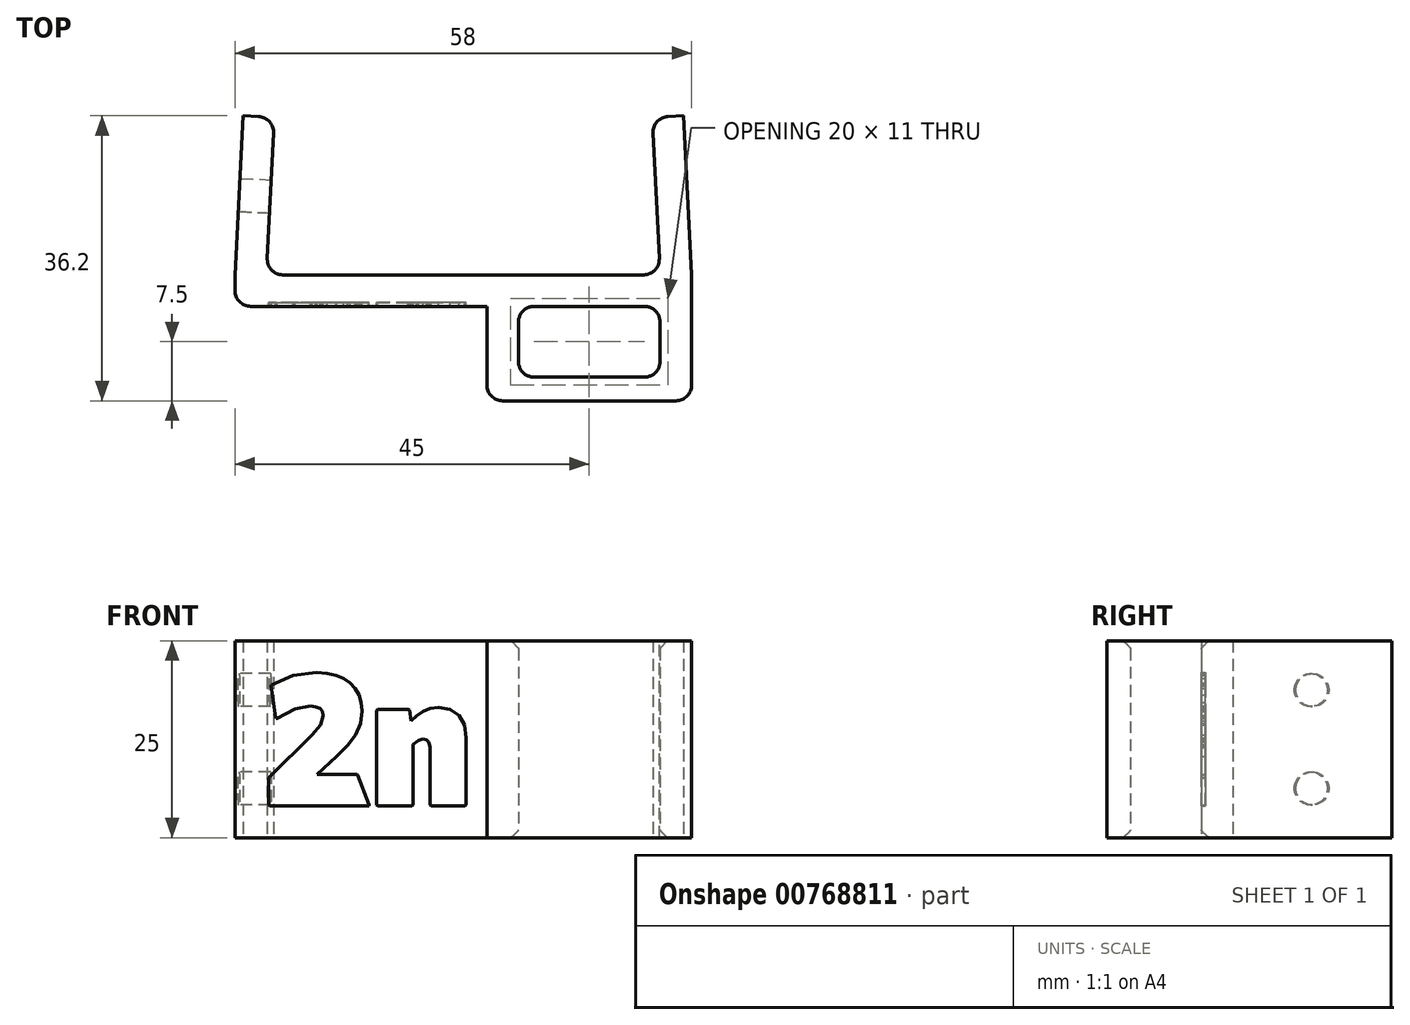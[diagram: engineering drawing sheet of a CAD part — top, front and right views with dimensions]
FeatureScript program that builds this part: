
annotation { "Feature Type Name" : "Feature", "Feature Type Description" : "" }
export const myFeature = defineFeature(function(context is Context, id is Id, definition is map)
    precondition{}
    {
        {
            var Q0;
            Q0=qCreatedBy(makeId("Top.planeOp"),FACE);
            var sketch = newSketch(context, id + "F0", { "sketchPlane" : qUnion([Q0])});
            skLineSegment(sketch, "E0", {"start": v(0, 0) * mm, "end": v(-25, 0) * mm});
            skLineSegment(sketch, "E1", {"start": v(-25, 0) * mm, "end": v(-24, 20) * mm});
            skLineSegment(sketch, "E2", {"start": v(0, 0) * mm, "end": v(0, 58.1) * mm, "construction": true});
            skLineSegment(sketch, "E3", {"start": v(-24, 20) * mm, "end": v(-28, 20.2) * mm});
            skLineSegment(sketch, "E4", {"start": v(-28, 20.2) * mm, "end": v(-29, 0) * mm});
            skLineSegment(sketch, "E5", {"start": v(-29, 0) * mm, "end": v(-29, -4) * mm});
            skLineSegment(sketch, "E6", {"start": v(-29, -4) * mm, "end": v(0, -4) * mm});
            skLineSegment(sketch, "E7.MirrorCS", {"start": v(25, 0) * mm, "end": v(24, 20) * mm});
            skLineSegment(sketch, "E8.MirrorCS", {"start": v(24, 20) * mm, "end": v(28, 20.2) * mm});
            skLineSegment(sketch, "E9.MirrorCS", {"start": v(28, 20.2) * mm, "end": v(29, 0) * mm});
            skLineSegment(sketch, "E10.MirrorCS", {"start": v(0, 0) * mm, "end": v(25, 0) * mm});
            skLineSegment(sketch, "E11.MirrorCS", {"start": v(29, 0) * mm, "end": v(29, -4) * mm});
            skPoint(sketch, "E12", {"position": v(25, -4) * mm});
            skPoint(sketch, "E13.second.point", {"position": v(10.6, -3) * mm});
            skPoint(sketch, "E13.third.point", {"position": v(18.98, -11.3) * mm});
            skLineSegment(sketch, "E14.trimOffspring", {"start": v(3, -4) * mm, "end": v(0, -4) * mm});
            skPoint(sketch, "E15.orphan", {"position": v(29, -4) * mm});
            skPoint(sketch, "E16", {"position": v(16, -3) * mm});
            skLineSegment(sketch, "E17", {"start": v(7, -4) * mm, "end": v(25, -4) * mm});
            skLineSegment(sketch, "E18", {"start": v(3, -4) * mm, "end": v(3, -16) * mm});
            skPoint(sketch, "E18.endSnap0", {"position": v(15, -16) * mm});
            skLineSegment(sketch, "E19", {"start": v(3, -16) * mm, "end": v(29, -16) * mm});
            skLineSegment(sketch, "E20", {"start": v(29, -4) * mm, "end": v(29, -16) * mm});
            skLineSegment(sketch, "E21", {"start": v(25, -4) * mm, "end": v(25, -13) * mm});
            skPoint(sketch, "E21.endSnap0", {"position": v(16, -13) * mm});
            skLineSegment(sketch, "E22", {"start": v(25, -13) * mm, "end": v(7, -13) * mm});
            skLineSegment(sketch, "E23", {"start": v(7, -13) * mm, "end": v(7, -4) * mm});
            skSolve(sketch);
        }
        {
            var Q0;
            Q0=makeQuery(id+"F0.imprint","IMPRINT",FACE,{"disambiguationData":[TD([[makeQuery(id+"F0.imprint","IMPRINT",EDGE,{"derivedFrom":sQuery(id+"F0.wireOp",EDGE,"E0")}),1.0]])]});
            extrude(context, id + "F1", {"entities" : qUnion([Q0]), "depth" : 25 * mm, "offsetDistance" : 25 * mm});
        }
        {
            var Q0;
            Q0=makeQuery(id+"F1.opExtrude","SWEPT_EDGE",EDGE,{"disambiguationData":[OSD([sQuery(id+"F0.wireOp",EDGE,"E0"),sQuery(id+"F0.wireOp",EDGE,"E1")])]});
            var Q1;
            Q1=makeQuery(id+"F1.opExtrude","SWEPT_EDGE",EDGE,{"disambiguationData":[OSD([sQuery(id+"F0.wireOp",EDGE,"E1"),sQuery(id+"F0.wireOp",EDGE,"E3")])]});
            var Q2;
            Q2=makeQuery(id+"F1.opExtrude","SWEPT_EDGE",EDGE,{"disambiguationData":[OSD([sQuery(id+"F0.wireOp",EDGE,"E7.MirrorCS"),sQuery(id+"F0.wireOp",EDGE,"E10.MirrorCS")])]});
            var Q3;
            Q3=makeQuery(id+"F1.opExtrude","SWEPT_EDGE",EDGE,{"disambiguationData":[OSD([sQuery(id+"F0.wireOp",EDGE,"E7.MirrorCS"),sQuery(id+"F0.wireOp",EDGE,"E8.MirrorCS")])]});
            var Q4;
            Q4=makeQuery(id+"F1.opExtrude","SWEPT_EDGE",EDGE,{"disambiguationData":[OSD([sQuery(id+"F0.wireOp",EDGE,"E5"),sQuery(id+"F0.wireOp",EDGE,"E6")])]});
            var Q5;
            Q5=makeQuery(id+"F1.opExtrude","SWEPT_EDGE",EDGE,{"disambiguationData":[OSD([sQuery(id+"F0.wireOp",EDGE,"e2a2dabb-557d-459b-9b9f-5adb2272a29e0.MirrorCS"),sQuery(id+"F0.wireOp",EDGE,"E11.MirrorCS")])]});
            var Q6;
            Q6=makeQuery(id+"F1.opExtrude","SWEPT_EDGE",EDGE,{"disambiguationData":[OSD([sQuery(id+"F0.wireOp",EDGE,"E18"),sQuery(id+"F0.wireOp",EDGE,"E19")])]});
            var Q7;
            Q7=makeQuery(id+"F1.opExtrude","SWEPT_EDGE",EDGE,{"disambiguationData":[OSD([sQuery(id+"F0.wireOp",EDGE,"E19"),sQuery(id+"F0.wireOp",EDGE,"E20")])]});
            var Q8;
            Q8=makeQuery(id+"F1.opExtrude","SWEPT_EDGE",EDGE,{"disambiguationData":[OSD([sQuery(id+"F0.wireOp",EDGE,"E17"),sQuery(id+"F0.wireOp",EDGE,"E21")])]});
            var Q9;
            Q9=makeQuery(id+"F1.opExtrude","SWEPT_EDGE",EDGE,{"disambiguationData":[OSD([sQuery(id+"F0.wireOp",EDGE,"E17"),sQuery(id+"F0.wireOp",EDGE,"E23")])]});
            var Q10;
            Q10=makeQuery(id+"F1.opExtrude","SWEPT_EDGE",EDGE,{"disambiguationData":[OSD([sQuery(id+"F0.wireOp",EDGE,"E21"),sQuery(id+"F0.wireOp",EDGE,"E22")])]});
            var Q11;
            Q11=makeQuery(id+"F1.opExtrude","SWEPT_EDGE",EDGE,{"disambiguationData":[OSD([sQuery(id+"F0.wireOp",EDGE,"E22"),sQuery(id+"F0.wireOp",EDGE,"E23")])]});
            fillet(context, id + "F2", {"entities" : qUnion([Q0, Q1, Q2, Q3, Q4, Q5, Q6, Q7, Q8, Q9, Q10, Q11]), "radius" : 2 * mm, "tangentPropagation" : true, "defaultsChanged" : false, "vertexSettings" : [], "allowEdgeOverflow" : false});
        }
        {
            var Q0;
            Q0=makeQuery(id+"F1.opExtrude","SWEPT_FACE",FACE,{"disambiguationData":[OSD([sQuery(id+"F0.wireOp",EDGE,"E6"),sQuery(id+"F0.wireOp",EDGE,"E14.trimOffspring")])]});
            var sketch = newSketch(context, id + "F3", { "sketchPlane" : qUnion([Q0])});
            skLineSegment(sketch, "E24", {"start": v(-13.28, 12.73) * mm, "end": v(-13.29, 12.73) * mm});
            skLineSegment(sketch, "E25", {"start": v(-13.29, 12.73) * mm, "end": v(-13.48, 12.73) * mm});
            skLineSegment(sketch, "E26", {"start": v(-13.48, 12.73) * mm, "end": v(-13.39, 12.82) * mm});
            skLineSegment(sketch, "E27", {"start": v(-13.39, 12.82) * mm, "end": v(-13.33, 12.87) * mm});
            skLineSegment(sketch, "E28", {"start": v(-13.33, 12.87) * mm, "end": v(-13.3, 12.93) * mm});
            skLineSegment(sketch, "E29", {"start": v(-13.3, 12.93) * mm, "end": v(-13.27, 12.98) * mm});
            skLineSegment(sketch, "E30", {"start": v(-13.27, 12.98) * mm, "end": v(-13.26, 13.04) * mm});
            skLineSegment(sketch, "E31", {"start": v(-13.26, 13.04) * mm, "end": v(-13.26, 13.08) * mm});
            skLineSegment(sketch, "E32", {"start": v(-13.26, 13.08) * mm, "end": v(-13.28, 13.12) * mm});
            skLineSegment(sketch, "E33", {"start": v(-13.28, 13.12) * mm, "end": v(-13.3, 13.15) * mm});
            skLineSegment(sketch, "E34", {"start": v(-13.3, 13.15) * mm, "end": v(-13.32, 13.18) * mm});
            skLineSegment(sketch, "E35", {"start": v(-13.32, 13.18) * mm, "end": v(-13.35, 13.2) * mm});
            skLineSegment(sketch, "E36", {"start": v(-13.35, 13.2) * mm, "end": v(-13.39, 13.22) * mm});
            skLineSegment(sketch, "E37", {"start": v(-13.39, 13.22) * mm, "end": v(-13.43, 13.23) * mm});
            skLineSegment(sketch, "E38", {"start": v(-13.43, 13.23) * mm, "end": v(-13.48, 13.23) * mm});
            skLineSegment(sketch, "E39", {"start": v(-13.48, 13.23) * mm, "end": v(-13.6, 13.22) * mm});
            skLineSegment(sketch, "E40", {"start": v(-13.6, 13.22) * mm, "end": v(-13.7, 13.17) * mm});
            skLineSegment(sketch, "E41", {"start": v(-13.7, 13.17) * mm, "end": v(-13.7, 13.17) * mm});
            skLineSegment(sketch, "E42", {"start": v(-13.7, 13.17) * mm, "end": v(-13.68, 13.01) * mm});
            skLineSegment(sketch, "E43", {"start": v(-13.68, 13.01) * mm, "end": v(-13.68, 13) * mm});
            skLineSegment(sketch, "E44", {"start": v(-13.68, 13) * mm, "end": v(-13.68, 13) * mm});
            skLineSegment(sketch, "E45", {"start": v(-13.68, 13) * mm, "end": v(-13.59, 13.05) * mm});
            skLineSegment(sketch, "E46", {"start": v(-13.59, 13.05) * mm, "end": v(-13.51, 13.07) * mm});
            skLineSegment(sketch, "E47", {"start": v(-13.51, 13.07) * mm, "end": v(-13.49, 13.06) * mm});
            skLineSegment(sketch, "E48", {"start": v(-13.49, 13.06) * mm, "end": v(-13.47, 13.05) * mm});
            skLineSegment(sketch, "E49", {"start": v(-13.47, 13.05) * mm, "end": v(-13.45, 13.04) * mm});
            skLineSegment(sketch, "E50", {"start": v(-13.45, 13.04) * mm, "end": v(-13.45, 13.02) * mm});
            skLineSegment(sketch, "E51", {"start": v(-13.45, 13.02) * mm, "end": v(-13.46, 12.97) * mm});
            skLineSegment(sketch, "E52", {"start": v(-13.46, 12.97) * mm, "end": v(-13.5, 12.92) * mm});
            skLineSegment(sketch, "E53", {"start": v(-13.5, 12.92) * mm, "end": v(-13.72, 12.72) * mm});
            skLineSegment(sketch, "E54", {"start": v(-13.72, 12.72) * mm, "end": v(-13.72, 12.71) * mm});
            skLineSegment(sketch, "E55", {"start": v(-13.72, 12.71) * mm, "end": v(-13.72, 12.58) * mm});
            skLineSegment(sketch, "E56", {"start": v(-13.72, 12.58) * mm, "end": v(-13.71, 12.58) * mm});
            skLineSegment(sketch, "E57", {"start": v(-13.71, 12.58) * mm, "end": v(-13.23, 12.58) * mm});
            skLineSegment(sketch, "E58", {"start": v(-13.23, 12.58) * mm, "end": v(-13.23, 12.58) * mm});
            skLineSegment(sketch, "E59", {"start": v(-13.23, 12.58) * mm, "end": v(-13.28, 12.73) * mm});
            skLineSegment(sketch, "E60", {"start": v(-12.89, 13.06) * mm, "end": v(-12.93, 13.05) * mm});
            skLineSegment(sketch, "E61", {"start": v(-12.93, 13.05) * mm, "end": v(-12.96, 13.04) * mm});
            skLineSegment(sketch, "E62", {"start": v(-12.96, 13.04) * mm, "end": v(-13, 13.02) * mm});
            skLineSegment(sketch, "E63", {"start": v(-13, 13.02) * mm, "end": v(-13.02, 13) * mm});
            skLineSegment(sketch, "E64", {"start": v(-13.02, 13) * mm, "end": v(-13.03, 13.05) * mm});
            skLineSegment(sketch, "E65", {"start": v(-13.03, 13.05) * mm, "end": v(-13.03, 13.05) * mm});
            skLineSegment(sketch, "E66", {"start": v(-13.03, 13.05) * mm, "end": v(-13.18, 13.05) * mm});
            skLineSegment(sketch, "E67", {"start": v(-13.18, 13.05) * mm, "end": v(-13.19, 13.05) * mm});
            skLineSegment(sketch, "E68", {"start": v(-13.19, 13.05) * mm, "end": v(-13.19, 12.58) * mm});
            skLineSegment(sketch, "E69", {"start": v(-13.19, 12.58) * mm, "end": v(-13.18, 12.58) * mm});
            skLineSegment(sketch, "E70", {"start": v(-13.18, 12.58) * mm, "end": v(-13.02, 12.58) * mm});
            skLineSegment(sketch, "E71", {"start": v(-13.02, 12.58) * mm, "end": v(-13.01, 12.58) * mm});
            skLineSegment(sketch, "E72", {"start": v(-13.01, 12.58) * mm, "end": v(-13.01, 12.88) * mm});
            skLineSegment(sketch, "E73", {"start": v(-13.01, 12.88) * mm, "end": v(-12.99, 12.9) * mm});
            skLineSegment(sketch, "E74", {"start": v(-12.99, 12.9) * mm, "end": v(-12.96, 12.9) * mm});
            skLineSegment(sketch, "E75", {"start": v(-12.96, 12.9) * mm, "end": v(-12.94, 12.9) * mm});
            skLineSegment(sketch, "E76", {"start": v(-12.94, 12.9) * mm, "end": v(-12.93, 12.9) * mm});
            skLineSegment(sketch, "E77", {"start": v(-12.93, 12.9) * mm, "end": v(-12.93, 12.88) * mm});
            skLineSegment(sketch, "E78", {"start": v(-12.93, 12.88) * mm, "end": v(-12.93, 12.86) * mm});
            skLineSegment(sketch, "E79", {"start": v(-12.93, 12.86) * mm, "end": v(-12.93, 12.58) * mm});
            skLineSegment(sketch, "E80", {"start": v(-12.93, 12.58) * mm, "end": v(-12.92, 12.58) * mm});
            skLineSegment(sketch, "E81", {"start": v(-12.92, 12.58) * mm, "end": v(-12.76, 12.58) * mm});
            skLineSegment(sketch, "E82", {"start": v(-12.76, 12.58) * mm, "end": v(-12.75, 12.58) * mm});
            skLineSegment(sketch, "E83", {"start": v(-12.75, 12.58) * mm, "end": v(-12.75, 12.91) * mm});
            skLineSegment(sketch, "E84", {"start": v(-12.75, 12.91) * mm, "end": v(-12.76, 12.97) * mm});
            skLineSegment(sketch, "E85", {"start": v(-12.76, 12.97) * mm, "end": v(-12.79, 13.02) * mm});
            skLineSegment(sketch, "E86", {"start": v(-12.79, 13.02) * mm, "end": v(-12.83, 13.05) * mm});
            skLineSegment(sketch, "E87", {"start": v(-12.83, 13.05) * mm, "end": v(-12.89, 13.06) * mm});
            skLineSegment(sketch, "E88", {"start": v(-12.6, 13.27) * mm, "end": v(-12.63, 13.26) * mm});
            skLineSegment(sketch, "E89", {"start": v(-12.63, 13.26) * mm, "end": v(-12.66, 13.25) * mm});
            skLineSegment(sketch, "E90", {"start": v(-12.66, 13.25) * mm, "end": v(-12.68, 13.22) * mm});
            skLineSegment(sketch, "E91", {"start": v(-12.68, 13.22) * mm, "end": v(-12.69, 13.18) * mm});
            skLineSegment(sketch, "E92", {"start": v(-12.69, 13.18) * mm, "end": v(-12.68, 13.14) * mm});
            skLineSegment(sketch, "E93", {"start": v(-12.68, 13.14) * mm, "end": v(-12.66, 13.11) * mm});
            skLineSegment(sketch, "E94", {"start": v(-12.66, 13.11) * mm, "end": v(-12.63, 13.1) * mm});
            skLineSegment(sketch, "E95", {"start": v(-12.63, 13.1) * mm, "end": v(-12.6, 13.09) * mm});
            skLineSegment(sketch, "E96", {"start": v(-12.6, 13.09) * mm, "end": v(-12.55, 13.1) * mm});
            skLineSegment(sketch, "E97", {"start": v(-12.55, 13.1) * mm, "end": v(-12.52, 13.11) * mm});
            skLineSegment(sketch, "E98", {"start": v(-12.52, 13.11) * mm, "end": v(-12.5, 13.14) * mm});
            skLineSegment(sketch, "E99", {"start": v(-12.5, 13.14) * mm, "end": v(-12.5, 13.18) * mm});
            skLineSegment(sketch, "E100", {"start": v(-12.5, 13.18) * mm, "end": v(-12.5, 13.22) * mm});
            skLineSegment(sketch, "E101", {"start": v(-12.5, 13.22) * mm, "end": v(-12.52, 13.25) * mm});
            skLineSegment(sketch, "E102", {"start": v(-12.52, 13.25) * mm, "end": v(-12.55, 13.26) * mm});
            skLineSegment(sketch, "E103", {"start": v(-12.55, 13.26) * mm, "end": v(-12.6, 13.27) * mm});
            skLineSegment(sketch, "E104", {"start": v(-12.5, 13.05) * mm, "end": v(-12.68, 13.05) * mm});
            skLineSegment(sketch, "E105", {"start": v(-12.68, 13.05) * mm, "end": v(-12.68, 13.05) * mm});
            skLineSegment(sketch, "E106", {"start": v(-12.68, 13.05) * mm, "end": v(-12.68, 12.58) * mm});
            skLineSegment(sketch, "E107", {"start": v(-12.68, 12.58) * mm, "end": v(-12.68, 12.58) * mm});
            skLineSegment(sketch, "E108", {"start": v(-12.68, 12.58) * mm, "end": v(-12.5, 12.58) * mm});
            skLineSegment(sketch, "E109", {"start": v(-12.5, 12.58) * mm, "end": v(-12.5, 12.58) * mm});
            skLineSegment(sketch, "E110", {"start": v(-12.5, 12.58) * mm, "end": v(-12.5, 13.05) * mm});
            skLineSegment(sketch, "E111", {"start": v(-12.5, 13.05) * mm, "end": v(-12.5, 13.05) * mm});
            skLineSegment(sketch, "E112", {"start": v(-11.96, 13.06) * mm, "end": v(-11.96, 13.06) * mm});
            skLineSegment(sketch, "E113", {"start": v(-11.96, 13.06) * mm, "end": v(-12.08, 13.01) * mm});
            skLineSegment(sketch, "E114", {"start": v(-12.08, 13.01) * mm, "end": v(-12.15, 13.05) * mm});
            skLineSegment(sketch, "E115", {"start": v(-12.15, 13.05) * mm, "end": v(-12.24, 13.06) * mm});
            skLineSegment(sketch, "E116", {"start": v(-12.24, 13.06) * mm, "end": v(-12.28, 13.05) * mm});
            skLineSegment(sketch, "E117", {"start": v(-12.28, 13.05) * mm, "end": v(-12.32, 13.05) * mm});
            skLineSegment(sketch, "E118", {"start": v(-12.32, 13.05) * mm, "end": v(-12.35, 13.03) * mm});
            skLineSegment(sketch, "E119", {"start": v(-12.35, 13.03) * mm, "end": v(-12.38, 13.01) * mm});
            skLineSegment(sketch, "E120", {"start": v(-12.38, 13.01) * mm, "end": v(-12.4, 12.99) * mm});
            skLineSegment(sketch, "E121", {"start": v(-12.4, 12.99) * mm, "end": v(-12.43, 12.96) * mm});
            skLineSegment(sketch, "E122", {"start": v(-12.43, 12.96) * mm, "end": v(-12.44, 12.92) * mm});
            skLineSegment(sketch, "E123", {"start": v(-12.44, 12.92) * mm, "end": v(-12.44, 12.89) * mm});
            skLineSegment(sketch, "E124", {"start": v(-12.44, 12.89) * mm, "end": v(-12.44, 12.85) * mm});
            skLineSegment(sketch, "E125", {"start": v(-12.44, 12.85) * mm, "end": v(-12.42, 12.8) * mm});
            skLineSegment(sketch, "E126", {"start": v(-12.42, 12.8) * mm, "end": v(-12.4, 12.78) * mm});
            skLineSegment(sketch, "E127", {"start": v(-12.4, 12.78) * mm, "end": v(-12.36, 12.75) * mm});
            skLineSegment(sketch, "E128", {"start": v(-12.36, 12.75) * mm, "end": v(-12.41, 12.71) * mm});
            skLineSegment(sketch, "E129", {"start": v(-12.41, 12.71) * mm, "end": v(-12.43, 12.66) * mm});
            skLineSegment(sketch, "E130", {"start": v(-12.43, 12.66) * mm, "end": v(-12.42, 12.64) * mm});
            skLineSegment(sketch, "E131", {"start": v(-12.42, 12.64) * mm, "end": v(-12.4, 12.61) * mm});
            skLineSegment(sketch, "E132", {"start": v(-12.4, 12.61) * mm, "end": v(-12.46, 12.57) * mm});
            skLineSegment(sketch, "E133", {"start": v(-12.46, 12.57) * mm, "end": v(-12.47, 12.52) * mm});
            skLineSegment(sketch, "E134", {"start": v(-12.47, 12.52) * mm, "end": v(-12.46, 12.47) * mm});
            skLineSegment(sketch, "E135", {"start": v(-12.46, 12.47) * mm, "end": v(-12.4, 12.44) * mm});
            skLineSegment(sketch, "E136", {"start": v(-12.4, 12.44) * mm, "end": v(-12.34, 12.42) * mm});
            skLineSegment(sketch, "E137", {"start": v(-12.34, 12.42) * mm, "end": v(-12.24, 12.4) * mm});
            skLineSegment(sketch, "E138", {"start": v(-12.24, 12.4) * mm, "end": v(-12.13, 12.42) * mm});
            skLineSegment(sketch, "E139", {"start": v(-12.13, 12.42) * mm, "end": v(-12.04, 12.46) * mm});
            skLineSegment(sketch, "E140", {"start": v(-12.04, 12.46) * mm, "end": v(-11.98, 12.52) * mm});
            skLineSegment(sketch, "E141", {"start": v(-11.98, 12.52) * mm, "end": v(-11.96, 12.59) * mm});
            skLineSegment(sketch, "E142", {"start": v(-11.96, 12.59) * mm, "end": v(-11.97, 12.63) * mm});
            skLineSegment(sketch, "E143", {"start": v(-11.97, 12.63) * mm, "end": v(-12, 12.67) * mm});
            skLineSegment(sketch, "E144", {"start": v(-12, 12.67) * mm, "end": v(-12.05, 12.69) * mm});
            skLineSegment(sketch, "E145", {"start": v(-12.05, 12.69) * mm, "end": v(-12.11, 12.7) * mm});
            skLineSegment(sketch, "E146", {"start": v(-12.11, 12.7) * mm, "end": v(-12.22, 12.7) * mm});
            skLineSegment(sketch, "E147", {"start": v(-12.22, 12.7) * mm, "end": v(-12.25, 12.7) * mm});
            skLineSegment(sketch, "E148", {"start": v(-12.25, 12.7) * mm, "end": v(-12.27, 12.7) * mm});
            skLineSegment(sketch, "E149", {"start": v(-12.27, 12.7) * mm, "end": v(-12.28, 12.71) * mm});
            skLineSegment(sketch, "E150", {"start": v(-12.28, 12.71) * mm, "end": v(-12.28, 12.72) * mm});
            skLineSegment(sketch, "E151", {"start": v(-12.28, 12.72) * mm, "end": v(-12.27, 12.73) * mm});
            skLineSegment(sketch, "E152", {"start": v(-12.27, 12.73) * mm, "end": v(-12.23, 12.73) * mm});
            skLineSegment(sketch, "E153", {"start": v(-12.23, 12.73) * mm, "end": v(-12.19, 12.73) * mm});
            skLineSegment(sketch, "E154", {"start": v(-12.19, 12.73) * mm, "end": v(-12.15, 12.74) * mm});
            skLineSegment(sketch, "E155", {"start": v(-12.15, 12.74) * mm, "end": v(-12.11, 12.76) * mm});
            skLineSegment(sketch, "E156", {"start": v(-12.11, 12.76) * mm, "end": v(-12.08, 12.77) * mm});
            skLineSegment(sketch, "E157", {"start": v(-12.08, 12.77) * mm, "end": v(-12.06, 12.8) * mm});
            skLineSegment(sketch, "E158", {"start": v(-12.06, 12.8) * mm, "end": v(-12.04, 12.83) * mm});
            skLineSegment(sketch, "E159", {"start": v(-12.04, 12.83) * mm, "end": v(-12.03, 12.86) * mm});
            skLineSegment(sketch, "E160", {"start": v(-12.03, 12.86) * mm, "end": v(-12.03, 12.9) * mm});
            skLineSegment(sketch, "E161", {"start": v(-12.03, 12.9) * mm, "end": v(-12.03, 12.93) * mm});
            skLineSegment(sketch, "E162", {"start": v(-12.03, 12.93) * mm, "end": v(-11.96, 12.93) * mm});
            skLineSegment(sketch, "E163", {"start": v(-11.96, 12.93) * mm, "end": v(-11.95, 12.93) * mm});
            skLineSegment(sketch, "E164", {"start": v(-11.95, 12.93) * mm, "end": v(-11.95, 12.93) * mm});
            skLineSegment(sketch, "E165", {"start": v(-11.95, 12.93) * mm, "end": v(-11.95, 13.06) * mm});
            skLineSegment(sketch, "E166", {"start": v(-11.95, 13.06) * mm, "end": v(-11.96, 13.06) * mm});
            skLineSegment(sketch, "E167", {"start": v(-12.18, 12.9) * mm, "end": v(-12.19, 12.87) * mm});
            skLineSegment(sketch, "E168", {"start": v(-12.19, 12.87) * mm, "end": v(-12.2, 12.85) * mm});
            skLineSegment(sketch, "E169", {"start": v(-12.2, 12.85) * mm, "end": v(-12.21, 12.84) * mm});
            skLineSegment(sketch, "E170", {"start": v(-12.21, 12.84) * mm, "end": v(-12.23, 12.83) * mm});
            skLineSegment(sketch, "E171", {"start": v(-12.23, 12.83) * mm, "end": v(-12.26, 12.84) * mm});
            skLineSegment(sketch, "E172", {"start": v(-12.26, 12.84) * mm, "end": v(-12.27, 12.85) * mm});
            skLineSegment(sketch, "E173", {"start": v(-12.27, 12.85) * mm, "end": v(-12.28, 12.87) * mm});
            skLineSegment(sketch, "E174", {"start": v(-12.28, 12.87) * mm, "end": v(-12.28, 12.9) * mm});
            skLineSegment(sketch, "E175", {"start": v(-12.28, 12.9) * mm, "end": v(-12.28, 12.91) * mm});
            skLineSegment(sketch, "E176", {"start": v(-12.28, 12.91) * mm, "end": v(-12.27, 12.94) * mm});
            skLineSegment(sketch, "E177", {"start": v(-12.27, 12.94) * mm, "end": v(-12.26, 12.95) * mm});
            skLineSegment(sketch, "E178", {"start": v(-12.26, 12.95) * mm, "end": v(-12.23, 12.96) * mm});
            skLineSegment(sketch, "E179", {"start": v(-12.23, 12.96) * mm, "end": v(-12.21, 12.95) * mm});
            skLineSegment(sketch, "E180", {"start": v(-12.21, 12.95) * mm, "end": v(-12.2, 12.94) * mm});
            skLineSegment(sketch, "E181", {"start": v(-12.2, 12.94) * mm, "end": v(-12.19, 12.92) * mm});
            skLineSegment(sketch, "E182", {"start": v(-12.19, 12.92) * mm, "end": v(-12.18, 12.9) * mm});
            skLineSegment(sketch, "E183", {"start": v(-12.23, 12.5) * mm, "end": v(-12.27, 12.5) * mm});
            skLineSegment(sketch, "E184", {"start": v(-12.27, 12.5) * mm, "end": v(-12.3, 12.5) * mm});
            skLineSegment(sketch, "E185", {"start": v(-12.3, 12.5) * mm, "end": v(-12.33, 12.52) * mm});
            skLineSegment(sketch, "E186", {"start": v(-12.33, 12.52) * mm, "end": v(-12.33, 12.54) * mm});
            skLineSegment(sketch, "E187", {"start": v(-12.33, 12.54) * mm, "end": v(-12.32, 12.57) * mm});
            skLineSegment(sketch, "E188", {"start": v(-12.32, 12.57) * mm, "end": v(-12.3, 12.57) * mm});
            skLineSegment(sketch, "E189", {"start": v(-12.3, 12.57) * mm, "end": v(-12.25, 12.57) * mm});
            skLineSegment(sketch, "E190", {"start": v(-12.25, 12.57) * mm, "end": v(-12.18, 12.56) * mm});
            skLineSegment(sketch, "E191", {"start": v(-12.18, 12.56) * mm, "end": v(-12.15, 12.56) * mm});
            skLineSegment(sketch, "E192", {"start": v(-12.15, 12.56) * mm, "end": v(-12.13, 12.56) * mm});
            skLineSegment(sketch, "E193", {"start": v(-12.13, 12.56) * mm, "end": v(-12.13, 12.55) * mm});
            skLineSegment(sketch, "E194", {"start": v(-12.13, 12.55) * mm, "end": v(-12.12, 12.54) * mm});
            skLineSegment(sketch, "E195", {"start": v(-12.12, 12.54) * mm, "end": v(-12.13, 12.52) * mm});
            skLineSegment(sketch, "E196", {"start": v(-12.13, 12.52) * mm, "end": v(-12.15, 12.5) * mm});
            skLineSegment(sketch, "E197", {"start": v(-12.15, 12.5) * mm, "end": v(-12.19, 12.5) * mm});
            skLineSegment(sketch, "E198", {"start": v(-12.19, 12.5) * mm, "end": v(-12.23, 12.5) * mm});
            skLineSegment(sketch, "E199", {"start": v(-11.62, 13.06) * mm, "end": v(-11.65, 13.06) * mm});
            skLineSegment(sketch, "E200", {"start": v(-11.65, 13.06) * mm, "end": v(-11.69, 13.04) * mm});
            skLineSegment(sketch, "E201", {"start": v(-11.69, 13.04) * mm, "end": v(-11.71, 13.03) * mm});
            skLineSegment(sketch, "E202", {"start": v(-11.71, 13.03) * mm, "end": v(-11.74, 13) * mm});
            skLineSegment(sketch, "E203", {"start": v(-11.74, 13) * mm, "end": v(-11.74, 13.26) * mm});
            skLineSegment(sketch, "E204", {"start": v(-11.74, 13.26) * mm, "end": v(-11.75, 13.26) * mm});
            skLineSegment(sketch, "E205", {"start": v(-11.75, 13.26) * mm, "end": v(-11.75, 13.26) * mm});
            skLineSegment(sketch, "E206", {"start": v(-11.75, 13.26) * mm, "end": v(-11.92, 13.24) * mm});
            skLineSegment(sketch, "E207", {"start": v(-11.92, 13.24) * mm, "end": v(-11.92, 13.23) * mm});
            skLineSegment(sketch, "E208", {"start": v(-11.92, 13.23) * mm, "end": v(-11.92, 12.58) * mm});
            skLineSegment(sketch, "E209", {"start": v(-11.92, 12.58) * mm, "end": v(-11.91, 12.58) * mm});
            skLineSegment(sketch, "E210", {"start": v(-11.91, 12.58) * mm, "end": v(-11.75, 12.58) * mm});
            skLineSegment(sketch, "E211", {"start": v(-11.75, 12.58) * mm, "end": v(-11.74, 12.58) * mm});
            skLineSegment(sketch, "E212", {"start": v(-11.74, 12.58) * mm, "end": v(-11.74, 12.88) * mm});
            skLineSegment(sketch, "E213", {"start": v(-11.74, 12.88) * mm, "end": v(-11.72, 12.9) * mm});
            skLineSegment(sketch, "E214", {"start": v(-11.72, 12.9) * mm, "end": v(-11.7, 12.9) * mm});
            skLineSegment(sketch, "E215", {"start": v(-11.7, 12.9) * mm, "end": v(-11.68, 12.9) * mm});
            skLineSegment(sketch, "E216", {"start": v(-11.68, 12.9) * mm, "end": v(-11.67, 12.9) * mm});
            skLineSegment(sketch, "E217", {"start": v(-11.67, 12.9) * mm, "end": v(-11.66, 12.88) * mm});
            skLineSegment(sketch, "E218", {"start": v(-11.66, 12.88) * mm, "end": v(-11.66, 12.86) * mm});
            skLineSegment(sketch, "E219", {"start": v(-11.66, 12.86) * mm, "end": v(-11.66, 12.58) * mm});
            skLineSegment(sketch, "E220", {"start": v(-11.66, 12.58) * mm, "end": v(-11.65, 12.58) * mm});
            skLineSegment(sketch, "E221", {"start": v(-11.65, 12.58) * mm, "end": v(-11.49, 12.58) * mm});
            skLineSegment(sketch, "E222", {"start": v(-11.49, 12.58) * mm, "end": v(-11.48, 12.58) * mm});
            skLineSegment(sketch, "E223", {"start": v(-11.48, 12.58) * mm, "end": v(-11.48, 12.91) * mm});
            skLineSegment(sketch, "E224", {"start": v(-11.48, 12.91) * mm, "end": v(-11.5, 12.97) * mm});
            skLineSegment(sketch, "E225", {"start": v(-11.5, 12.97) * mm, "end": v(-11.52, 13.02) * mm});
            skLineSegment(sketch, "E226", {"start": v(-11.52, 13.02) * mm, "end": v(-11.56, 13.05) * mm});
            skLineSegment(sketch, "E227", {"start": v(-11.56, 13.05) * mm, "end": v(-11.62, 13.06) * mm});
            skLineSegment(sketch, "E228", {"start": v(-11.12, 12.72) * mm, "end": v(-11.13, 12.73) * mm});
            skLineSegment(sketch, "E229", {"start": v(-11.13, 12.73) * mm, "end": v(-11.13, 12.73) * mm});
            skLineSegment(sketch, "E230", {"start": v(-11.13, 12.73) * mm, "end": v(-11.16, 12.72) * mm});
            skLineSegment(sketch, "E231", {"start": v(-11.16, 12.72) * mm, "end": v(-11.18, 12.73) * mm});
            skLineSegment(sketch, "E232", {"start": v(-11.18, 12.73) * mm, "end": v(-11.2, 12.73) * mm});
            skLineSegment(sketch, "E233", {"start": v(-11.2, 12.73) * mm, "end": v(-11.2, 12.75) * mm});
            skLineSegment(sketch, "E234", {"start": v(-11.2, 12.75) * mm, "end": v(-11.2, 12.77) * mm});
            skLineSegment(sketch, "E235", {"start": v(-11.2, 12.77) * mm, "end": v(-11.2, 12.9) * mm});
            skLineSegment(sketch, "E236", {"start": v(-11.2, 12.9) * mm, "end": v(-11.12, 12.9) * mm});
            skLineSegment(sketch, "E237", {"start": v(-11.12, 12.9) * mm, "end": v(-11.12, 12.91) * mm});
            skLineSegment(sketch, "E238", {"start": v(-11.12, 12.91) * mm, "end": v(-11.12, 13.07) * mm});
            skLineSegment(sketch, "E239", {"start": v(-11.12, 13.07) * mm, "end": v(-11.12, 13.07) * mm});
            skLineSegment(sketch, "E240", {"start": v(-11.12, 13.07) * mm, "end": v(-11.21, 13.05) * mm});
            skLineSegment(sketch, "E241", {"start": v(-11.21, 13.05) * mm, "end": v(-11.21, 13.2) * mm});
            skLineSegment(sketch, "E242", {"start": v(-11.21, 13.2) * mm, "end": v(-11.21, 13.2) * mm});
            skLineSegment(sketch, "E243", {"start": v(-11.21, 13.2) * mm, "end": v(-11.22, 13.2) * mm});
            skLineSegment(sketch, "E244", {"start": v(-11.22, 13.2) * mm, "end": v(-11.38, 13.18) * mm});
            skLineSegment(sketch, "E245", {"start": v(-11.38, 13.18) * mm, "end": v(-11.39, 13.18) * mm});
            skLineSegment(sketch, "E246", {"start": v(-11.39, 13.18) * mm, "end": v(-11.39, 13.02) * mm});
            skLineSegment(sketch, "E247", {"start": v(-11.39, 13.02) * mm, "end": v(-11.44, 13.01) * mm});
            skLineSegment(sketch, "E248", {"start": v(-11.44, 13.01) * mm, "end": v(-11.44, 13) * mm});
            skLineSegment(sketch, "E249", {"start": v(-11.44, 13) * mm, "end": v(-11.44, 12.91) * mm});
            skLineSegment(sketch, "E250", {"start": v(-11.44, 12.91) * mm, "end": v(-11.44, 12.9) * mm});
            skLineSegment(sketch, "E251", {"start": v(-11.44, 12.9) * mm, "end": v(-11.39, 12.9) * mm});
            skLineSegment(sketch, "E252", {"start": v(-11.39, 12.9) * mm, "end": v(-11.39, 12.74) * mm});
            skLineSegment(sketch, "E253", {"start": v(-11.39, 12.74) * mm, "end": v(-11.37, 12.67) * mm});
            skLineSegment(sketch, "E254", {"start": v(-11.37, 12.67) * mm, "end": v(-11.34, 12.62) * mm});
            skLineSegment(sketch, "E255", {"start": v(-11.34, 12.62) * mm, "end": v(-11.28, 12.58) * mm});
            skLineSegment(sketch, "E256", {"start": v(-11.28, 12.58) * mm, "end": v(-11.2, 12.57) * mm});
            skLineSegment(sketch, "E257", {"start": v(-11.2, 12.57) * mm, "end": v(-11.15, 12.58) * mm});
            skLineSegment(sketch, "E258", {"start": v(-11.15, 12.58) * mm, "end": v(-11.1, 12.59) * mm});
            skLineSegment(sketch, "E259", {"start": v(-11.1, 12.59) * mm, "end": v(-11.1, 12.6) * mm});
            skLineSegment(sketch, "E260", {"start": v(-11.1, 12.6) * mm, "end": v(-11.12, 12.72) * mm});
            skLineSegment(sketch, "E261", {"start": v(-10.84, 12.66) * mm, "end": v(-10.84, 12.63) * mm});
            skLineSegment(sketch, "E262", {"start": v(-10.84, 12.63) * mm, "end": v(-10.86, 12.6) * mm});
            skLineSegment(sketch, "E263", {"start": v(-10.86, 12.6) * mm, "end": v(-10.89, 12.59) * mm});
            skLineSegment(sketch, "E264", {"start": v(-10.89, 12.59) * mm, "end": v(-10.92, 12.58) * mm});
            skLineSegment(sketch, "E265", {"start": v(-10.92, 12.58) * mm, "end": v(-10.95, 12.59) * mm});
            skLineSegment(sketch, "E266", {"start": v(-10.95, 12.59) * mm, "end": v(-10.97, 12.6) * mm});
            skLineSegment(sketch, "E267", {"start": v(-10.97, 12.6) * mm, "end": v(-11, 12.63) * mm});
            skLineSegment(sketch, "E268", {"start": v(-11, 12.63) * mm, "end": v(-11, 12.66) * mm});
            skLineSegment(sketch, "E269", {"start": v(-11, 12.66) * mm, "end": v(-11, 12.7) * mm});
            skLineSegment(sketch, "E270", {"start": v(-11, 12.7) * mm, "end": v(-10.97, 12.72) * mm});
            skLineSegment(sketch, "E271", {"start": v(-10.97, 12.72) * mm, "end": v(-10.95, 12.74) * mm});
            skLineSegment(sketch, "E272", {"start": v(-10.95, 12.74) * mm, "end": v(-10.92, 12.74) * mm});
            skLineSegment(sketch, "E273", {"start": v(-10.92, 12.74) * mm, "end": v(-10.89, 12.74) * mm});
            skLineSegment(sketch, "E274", {"start": v(-10.89, 12.74) * mm, "end": v(-10.86, 12.72) * mm});
            skLineSegment(sketch, "E275", {"start": v(-10.86, 12.72) * mm, "end": v(-10.84, 12.7) * mm});
            skLineSegment(sketch, "E276", {"start": v(-10.84, 12.7) * mm, "end": v(-10.84, 12.66) * mm});
            skSolve(sketch);
        }
        {
            var Q0;
            Q0=makeQuery(id+"F3.imprint","IMPRINT",FACE,{"disambiguationData":[TD([[makeQuery(id+"F3.imprint","IMPRINT",EDGE,{"derivedFrom":sQuery(id+"F3.wireOp",EDGE,"E24")}),1.0]])]});
            var Q1;
            Q1=makeQuery(id+"F3.imprint","IMPRINT",FACE,{"disambiguationData":[TD([[makeQuery(id+"F3.imprint","IMPRINT",EDGE,{"derivedFrom":sQuery(id+"F3.wireOp",EDGE,"E60")}),1.0]])]});
            var Q2;
            Q2=makeQuery(id+"F3.imprint","IMPRINT",FACE,{"disambiguationData":[TD([[makeQuery(id+"F3.imprint","IMPRINT",EDGE,{"derivedFrom":sQuery(id+"F3.wireOp",EDGE,"E104")}),1.0]])]});
            var Q3;
            Q3=makeQuery(id+"F3.imprint","IMPRINT",FACE,{"disambiguationData":[TD([[makeQuery(id+"F3.imprint","IMPRINT",EDGE,{"derivedFrom":sQuery(id+"F3.wireOp",EDGE,"E88")}),1.0]])]});
            var Q4;
            Q4=makeQuery(id+"F3.imprint","IMPRINT",FACE,{"disambiguationData":[TD([[makeQuery(id+"F3.imprint","IMPRINT",EDGE,{"derivedFrom":sQuery(id+"F3.wireOp",EDGE,"E112")}),1.0]])]});
            var Q5;
            Q5=makeQuery(id+"F3.imprint","IMPRINT",FACE,{"disambiguationData":[TD([[makeQuery(id+"F3.imprint","IMPRINT",EDGE,{"derivedFrom":sQuery(id+"F3.wireOp",EDGE,"E199")}),1.0]])]});
            var Q6;
            Q6=makeQuery(id+"F3.imprint","IMPRINT",FACE,{"disambiguationData":[TD([[makeQuery(id+"F3.imprint","IMPRINT",EDGE,{"derivedFrom":sQuery(id+"F3.wireOp",EDGE,"E228")}),1.0]])]});
            var Q7;
            Q7=makeQuery(id+"F3.imprint","IMPRINT",FACE,{"disambiguationData":[TD([[makeQuery(id+"F3.imprint","IMPRINT",EDGE,{"derivedFrom":sQuery(id+"F3.wireOp",EDGE,"E261")}),-1.0]])]});
            extrude(context, id + "F4", {"entities" : qUnion([Q0, Q1, Q2, Q3, Q4, Q5, Q6, Q7]), "depth" : 5 * mm, "offsetDistance" : 25 * mm});
        }
        {
            var Q0;
            Q0=makeQuery(id+"F4.opExtrude","SWEPT_BODY",BODY,{"disambiguationData":[OSD([sQuery(id+"F3.wireOp",EDGE,"E228"),sQuery(id+"F3.wireOp",EDGE,"E229"),sQuery(id+"F3.wireOp",EDGE,"E230"),sQuery(id+"F3.wireOp",EDGE,"E231"),sQuery(id+"F3.wireOp",EDGE,"E232"),sQuery(id+"F3.wireOp",EDGE,"E233"),sQuery(id+"F3.wireOp",EDGE,"E234"),sQuery(id+"F3.wireOp",EDGE,"E235"),sQuery(id+"F3.wireOp",EDGE,"E236"),sQuery(id+"F3.wireOp",EDGE,"E237"),sQuery(id+"F3.wireOp",EDGE,"E238"),sQuery(id+"F3.wireOp",EDGE,"E239"),sQuery(id+"F3.wireOp",EDGE,"E239"),sQuery(id+"F3.wireOp",EDGE,"E240"),sQuery(id+"F3.wireOp",EDGE,"E241"),sQuery(id+"F3.wireOp",EDGE,"E242"),sQuery(id+"F3.wireOp",EDGE,"E243"),sQuery(id+"F3.wireOp",EDGE,"E244"),sQuery(id+"F3.wireOp",EDGE,"E245"),sQuery(id+"F3.wireOp",EDGE,"E246"),sQuery(id+"F3.wireOp",EDGE,"E247"),sQuery(id+"F3.wireOp",EDGE,"E248"),sQuery(id+"F3.wireOp",EDGE,"E249"),sQuery(id+"F3.wireOp",EDGE,"E250"),sQuery(id+"F3.wireOp",EDGE,"E251"),sQuery(id+"F3.wireOp",EDGE,"E252"),sQuery(id+"F3.wireOp",EDGE,"E253"),sQuery(id+"F3.wireOp",EDGE,"E254"),sQuery(id+"F3.wireOp",EDGE,"E255"),sQuery(id+"F3.wireOp",EDGE,"E256"),sQuery(id+"F3.wireOp",EDGE,"E257"),sQuery(id+"F3.wireOp",EDGE,"E258"),sQuery(id+"F3.wireOp",EDGE,"E259"),sQuery(id+"F3.wireOp",EDGE,"E260")])]});
            var Q1;
            Q1=makeQuery(id+"F4.opExtrude","SWEPT_BODY",BODY,{"disambiguationData":[OSD([sQuery(id+"F3.wireOp",EDGE,"E261"),sQuery(id+"F3.wireOp",EDGE,"E262"),sQuery(id+"F3.wireOp",EDGE,"E263"),sQuery(id+"F3.wireOp",EDGE,"E264"),sQuery(id+"F3.wireOp",EDGE,"E265"),sQuery(id+"F3.wireOp",EDGE,"E266"),sQuery(id+"F3.wireOp",EDGE,"E267"),sQuery(id+"F3.wireOp",EDGE,"E268"),sQuery(id+"F3.wireOp",EDGE,"E269"),sQuery(id+"F3.wireOp",EDGE,"E270"),sQuery(id+"F3.wireOp",EDGE,"E271"),sQuery(id+"F3.wireOp",EDGE,"E272"),sQuery(id+"F3.wireOp",EDGE,"E273"),sQuery(id+"F3.wireOp",EDGE,"E274"),sQuery(id+"F3.wireOp",EDGE,"E275"),sQuery(id+"F3.wireOp",EDGE,"E276")])]});
            var Q2;
            Q2=makeQuery(id+"F4.opExtrude","SWEPT_BODY",BODY,{"disambiguationData":[OSD([sQuery(id+"F3.wireOp",EDGE,"E60"),sQuery(id+"F3.wireOp",EDGE,"E61"),sQuery(id+"F3.wireOp",EDGE,"E62"),sQuery(id+"F3.wireOp",EDGE,"E63"),sQuery(id+"F3.wireOp",EDGE,"E64"),sQuery(id+"F3.wireOp",EDGE,"E65"),sQuery(id+"F3.wireOp",EDGE,"E66"),sQuery(id+"F3.wireOp",EDGE,"E67"),sQuery(id+"F3.wireOp",EDGE,"E68"),sQuery(id+"F3.wireOp",EDGE,"E69"),sQuery(id+"F3.wireOp",EDGE,"E70"),sQuery(id+"F3.wireOp",EDGE,"E71"),sQuery(id+"F3.wireOp",EDGE,"E72"),sQuery(id+"F3.wireOp",EDGE,"E73"),sQuery(id+"F3.wireOp",EDGE,"E74"),sQuery(id+"F3.wireOp",EDGE,"E75"),sQuery(id+"F3.wireOp",EDGE,"E76"),sQuery(id+"F3.wireOp",EDGE,"E77"),sQuery(id+"F3.wireOp",EDGE,"E78"),sQuery(id+"F3.wireOp",EDGE,"E79"),sQuery(id+"F3.wireOp",EDGE,"E80"),sQuery(id+"F3.wireOp",EDGE,"E81"),sQuery(id+"F3.wireOp",EDGE,"E82"),sQuery(id+"F3.wireOp",EDGE,"E83"),sQuery(id+"F3.wireOp",EDGE,"E84"),sQuery(id+"F3.wireOp",EDGE,"E85"),sQuery(id+"F3.wireOp",EDGE,"E86"),sQuery(id+"F3.wireOp",EDGE,"E87")])]});
            var Q3;
            Q3=makeQuery(id+"F4.opExtrude","SWEPT_BODY",BODY,{"disambiguationData":[OSD([sQuery(id+"F3.wireOp",EDGE,"E112"),sQuery(id+"F3.wireOp",EDGE,"E113"),sQuery(id+"F3.wireOp",EDGE,"E114"),sQuery(id+"F3.wireOp",EDGE,"E115"),sQuery(id+"F3.wireOp",EDGE,"E116"),sQuery(id+"F3.wireOp",EDGE,"E117"),sQuery(id+"F3.wireOp",EDGE,"E118"),sQuery(id+"F3.wireOp",EDGE,"E119"),sQuery(id+"F3.wireOp",EDGE,"E120"),sQuery(id+"F3.wireOp",EDGE,"E121"),sQuery(id+"F3.wireOp",EDGE,"E122"),sQuery(id+"F3.wireOp",EDGE,"E123"),sQuery(id+"F3.wireOp",EDGE,"E124"),sQuery(id+"F3.wireOp",EDGE,"E125"),sQuery(id+"F3.wireOp",EDGE,"E126"),sQuery(id+"F3.wireOp",EDGE,"E127"),sQuery(id+"F3.wireOp",EDGE,"E128"),sQuery(id+"F3.wireOp",EDGE,"E129"),sQuery(id+"F3.wireOp",EDGE,"E130"),sQuery(id+"F3.wireOp",EDGE,"E131"),sQuery(id+"F3.wireOp",EDGE,"E132"),sQuery(id+"F3.wireOp",EDGE,"E133"),sQuery(id+"F3.wireOp",EDGE,"E134"),sQuery(id+"F3.wireOp",EDGE,"E135"),sQuery(id+"F3.wireOp",EDGE,"E136"),sQuery(id+"F3.wireOp",EDGE,"E137"),sQuery(id+"F3.wireOp",EDGE,"E138"),sQuery(id+"F3.wireOp",EDGE,"E139"),sQuery(id+"F3.wireOp",EDGE,"E140"),sQuery(id+"F3.wireOp",EDGE,"E141"),sQuery(id+"F3.wireOp",EDGE,"E142"),sQuery(id+"F3.wireOp",EDGE,"E143"),sQuery(id+"F3.wireOp",EDGE,"E144"),sQuery(id+"F3.wireOp",EDGE,"E145"),sQuery(id+"F3.wireOp",EDGE,"E146"),sQuery(id+"F3.wireOp",EDGE,"E147"),sQuery(id+"F3.wireOp",EDGE,"E148"),sQuery(id+"F3.wireOp",EDGE,"E149"),sQuery(id+"F3.wireOp",EDGE,"E150"),sQuery(id+"F3.wireOp",EDGE,"E151"),sQuery(id+"F3.wireOp",EDGE,"E152"),sQuery(id+"F3.wireOp",EDGE,"E153"),sQuery(id+"F3.wireOp",EDGE,"E154"),sQuery(id+"F3.wireOp",EDGE,"E155"),sQuery(id+"F3.wireOp",EDGE,"E156"),sQuery(id+"F3.wireOp",EDGE,"E157"),sQuery(id+"F3.wireOp",EDGE,"E158"),sQuery(id+"F3.wireOp",EDGE,"E159"),sQuery(id+"F3.wireOp",EDGE,"E160"),sQuery(id+"F3.wireOp",EDGE,"E161"),sQuery(id+"F3.wireOp",EDGE,"E162"),sQuery(id+"F3.wireOp",EDGE,"E163"),sQuery(id+"F3.wireOp",EDGE,"E164"),sQuery(id+"F3.wireOp",EDGE,"E165"),sQuery(id+"F3.wireOp",EDGE,"E166"),sQuery(id+"F3.wireOp",EDGE,"E167"),sQuery(id+"F3.wireOp",EDGE,"E168"),sQuery(id+"F3.wireOp",EDGE,"E169"),sQuery(id+"F3.wireOp",EDGE,"E170"),sQuery(id+"F3.wireOp",EDGE,"E171"),sQuery(id+"F3.wireOp",EDGE,"E172"),sQuery(id+"F3.wireOp",EDGE,"E173"),sQuery(id+"F3.wireOp",EDGE,"E174"),sQuery(id+"F3.wireOp",EDGE,"E175"),sQuery(id+"F3.wireOp",EDGE,"E176"),sQuery(id+"F3.wireOp",EDGE,"E177"),sQuery(id+"F3.wireOp",EDGE,"E178"),sQuery(id+"F3.wireOp",EDGE,"E179"),sQuery(id+"F3.wireOp",EDGE,"E180"),sQuery(id+"F3.wireOp",EDGE,"E181"),sQuery(id+"F3.wireOp",EDGE,"E182"),sQuery(id+"F3.wireOp",EDGE,"E183"),sQuery(id+"F3.wireOp",EDGE,"E184"),sQuery(id+"F3.wireOp",EDGE,"E185"),sQuery(id+"F3.wireOp",EDGE,"E186"),sQuery(id+"F3.wireOp",EDGE,"E187"),sQuery(id+"F3.wireOp",EDGE,"E188"),sQuery(id+"F3.wireOp",EDGE,"E189"),sQuery(id+"F3.wireOp",EDGE,"E190"),sQuery(id+"F3.wireOp",EDGE,"E191"),sQuery(id+"F3.wireOp",EDGE,"E192"),sQuery(id+"F3.wireOp",EDGE,"E193"),sQuery(id+"F3.wireOp",EDGE,"E194"),sQuery(id+"F3.wireOp",EDGE,"E195"),sQuery(id+"F3.wireOp",EDGE,"E196"),sQuery(id+"F3.wireOp",EDGE,"E197"),sQuery(id+"F3.wireOp",EDGE,"E198")])]});
            var Q4;
            Q4=makeQuery(id+"F4.opExtrude","SWEPT_BODY",BODY,{"disambiguationData":[OSD([sQuery(id+"F3.wireOp",EDGE,"E199"),sQuery(id+"F3.wireOp",EDGE,"E200"),sQuery(id+"F3.wireOp",EDGE,"E201"),sQuery(id+"F3.wireOp",EDGE,"E202"),sQuery(id+"F3.wireOp",EDGE,"E203"),sQuery(id+"F3.wireOp",EDGE,"E204"),sQuery(id+"F3.wireOp",EDGE,"E205"),sQuery(id+"F3.wireOp",EDGE,"E206"),sQuery(id+"F3.wireOp",EDGE,"E207"),sQuery(id+"F3.wireOp",EDGE,"E208"),sQuery(id+"F3.wireOp",EDGE,"E209"),sQuery(id+"F3.wireOp",EDGE,"E210"),sQuery(id+"F3.wireOp",EDGE,"E211"),sQuery(id+"F3.wireOp",EDGE,"E212"),sQuery(id+"F3.wireOp",EDGE,"E213"),sQuery(id+"F3.wireOp",EDGE,"E214"),sQuery(id+"F3.wireOp",EDGE,"E215"),sQuery(id+"F3.wireOp",EDGE,"E216"),sQuery(id+"F3.wireOp",EDGE,"E217"),sQuery(id+"F3.wireOp",EDGE,"E218"),sQuery(id+"F3.wireOp",EDGE,"E219"),sQuery(id+"F3.wireOp",EDGE,"E220"),sQuery(id+"F3.wireOp",EDGE,"E221"),sQuery(id+"F3.wireOp",EDGE,"E222"),sQuery(id+"F3.wireOp",EDGE,"E223"),sQuery(id+"F3.wireOp",EDGE,"E224"),sQuery(id+"F3.wireOp",EDGE,"E225"),sQuery(id+"F3.wireOp",EDGE,"E226"),sQuery(id+"F3.wireOp",EDGE,"E227")])]});
            var Q5;
            Q5=makeQuery(id+"F4.opExtrude","SWEPT_BODY",BODY,{"disambiguationData":[OSD([sQuery(id+"F3.wireOp",EDGE,"E24"),sQuery(id+"F3.wireOp",EDGE,"E25"),sQuery(id+"F3.wireOp",EDGE,"E26"),sQuery(id+"F3.wireOp",EDGE,"E27"),sQuery(id+"F3.wireOp",EDGE,"E28"),sQuery(id+"F3.wireOp",EDGE,"E29"),sQuery(id+"F3.wireOp",EDGE,"E30"),sQuery(id+"F3.wireOp",EDGE,"E31"),sQuery(id+"F3.wireOp",EDGE,"E32"),sQuery(id+"F3.wireOp",EDGE,"E33"),sQuery(id+"F3.wireOp",EDGE,"E34"),sQuery(id+"F3.wireOp",EDGE,"E35"),sQuery(id+"F3.wireOp",EDGE,"E36"),sQuery(id+"F3.wireOp",EDGE,"E37"),sQuery(id+"F3.wireOp",EDGE,"E38"),sQuery(id+"F3.wireOp",EDGE,"E39"),sQuery(id+"F3.wireOp",EDGE,"E40"),sQuery(id+"F3.wireOp",EDGE,"E41"),sQuery(id+"F3.wireOp",EDGE,"E42"),sQuery(id+"F3.wireOp",EDGE,"E43"),sQuery(id+"F3.wireOp",EDGE,"E44"),sQuery(id+"F3.wireOp",EDGE,"E45"),sQuery(id+"F3.wireOp",EDGE,"E46"),sQuery(id+"F3.wireOp",EDGE,"E47"),sQuery(id+"F3.wireOp",EDGE,"E48"),sQuery(id+"F3.wireOp",EDGE,"E49"),sQuery(id+"F3.wireOp",EDGE,"E50"),sQuery(id+"F3.wireOp",EDGE,"E51"),sQuery(id+"F3.wireOp",EDGE,"E52"),sQuery(id+"F3.wireOp",EDGE,"E53"),sQuery(id+"F3.wireOp",EDGE,"E54"),sQuery(id+"F3.wireOp",EDGE,"E55"),sQuery(id+"F3.wireOp",EDGE,"E56"),sQuery(id+"F3.wireOp",EDGE,"E57"),sQuery(id+"F3.wireOp",EDGE,"E58"),sQuery(id+"F3.wireOp",EDGE,"E58"),sQuery(id+"F3.wireOp",EDGE,"E59")])]});
            var Q6;
            Q6=makeQuery(id+"F4.opExtrude","SWEPT_BODY",BODY,{"disambiguationData":[OSD([sQuery(id+"F3.wireOp",EDGE,"E104"),sQuery(id+"F3.wireOp",EDGE,"E105"),sQuery(id+"F3.wireOp",EDGE,"E106"),sQuery(id+"F3.wireOp",EDGE,"E107"),sQuery(id+"F3.wireOp",EDGE,"E108"),sQuery(id+"F3.wireOp",EDGE,"E109"),sQuery(id+"F3.wireOp",EDGE,"E110"),sQuery(id+"F3.wireOp",EDGE,"E111")])]});
            var Q7;
            Q7=makeQuery(id+"F4.opExtrude","SWEPT_BODY",BODY,{"disambiguationData":[OSD([sQuery(id+"F3.wireOp",EDGE,"E88"),sQuery(id+"F3.wireOp",EDGE,"E89"),sQuery(id+"F3.wireOp",EDGE,"E90"),sQuery(id+"F3.wireOp",EDGE,"E91"),sQuery(id+"F3.wireOp",EDGE,"E92"),sQuery(id+"F3.wireOp",EDGE,"E93"),sQuery(id+"F3.wireOp",EDGE,"E94"),sQuery(id+"F3.wireOp",EDGE,"E95"),sQuery(id+"F3.wireOp",EDGE,"E96"),sQuery(id+"F3.wireOp",EDGE,"E97"),sQuery(id+"F3.wireOp",EDGE,"E98"),sQuery(id+"F3.wireOp",EDGE,"E99"),sQuery(id+"F3.wireOp",EDGE,"E100"),sQuery(id+"F3.wireOp",EDGE,"E101"),sQuery(id+"F3.wireOp",EDGE,"E102"),sQuery(id+"F3.wireOp",EDGE,"E103")])]});
            var Q8;
            Q8=makeQuery(id+"F4.opExtrude","CAP_VERTEX",VERTEX,{"disambiguationData":[OSD([sQuery(id+"F3.wireOp",EDGE,"E55"),sQuery(id+"F3.wireOp",EDGE,"E56")])],"isStart":false});
            transform(context, id + "F5", {"entities" : qUnion([Q0, Q1, Q2, Q3, Q4, Q5, Q6, Q7]), "transformType" : TransformType.SCALE_UNIFORMLY, "scale" : 10, "scalePoint" : qUnion([Q8]), "makeCopy" : false});
        }
        {
            var Q0;
            Q0=makeQuery(id+"F4.opExtrude","SWEPT_FACE",FACE,{"disambiguationData":[OSD([sQuery(id+"F3.wireOp",EDGE,"E57")])]});
            var sketch = newSketch(context, id + "F6", { "sketchPlane" : qUnion([Q0])});
            skPoint(sketch, "E277.0", {"position": v(-27, 4) * mm});
            skLineSegment(sketch, "E278", {"start": v(-13.66, -41) * mm, "end": v(-27, 4) * mm, "construction": true});
            skSolve(sketch);
        }
        {
            var Q0;
            Q0=makeQuery(id+"F4.opExtrude","SWEPT_BODY",BODY,{"disambiguationData":[OSD([sQuery(id+"F3.wireOp",EDGE,"E261"),sQuery(id+"F3.wireOp",EDGE,"E262"),sQuery(id+"F3.wireOp",EDGE,"E263"),sQuery(id+"F3.wireOp",EDGE,"E264"),sQuery(id+"F3.wireOp",EDGE,"E265"),sQuery(id+"F3.wireOp",EDGE,"E266"),sQuery(id+"F3.wireOp",EDGE,"E267"),sQuery(id+"F3.wireOp",EDGE,"E268"),sQuery(id+"F3.wireOp",EDGE,"E269"),sQuery(id+"F3.wireOp",EDGE,"E270"),sQuery(id+"F3.wireOp",EDGE,"E271"),sQuery(id+"F3.wireOp",EDGE,"E272"),sQuery(id+"F3.wireOp",EDGE,"E273"),sQuery(id+"F3.wireOp",EDGE,"E274"),sQuery(id+"F3.wireOp",EDGE,"E275"),sQuery(id+"F3.wireOp",EDGE,"E276")])]});
            var Q1;
            Q1=makeQuery(id+"F4.opExtrude","SWEPT_BODY",BODY,{"disambiguationData":[OSD([sQuery(id+"F3.wireOp",EDGE,"E24"),sQuery(id+"F3.wireOp",EDGE,"E25"),sQuery(id+"F3.wireOp",EDGE,"E26"),sQuery(id+"F3.wireOp",EDGE,"E27"),sQuery(id+"F3.wireOp",EDGE,"E28"),sQuery(id+"F3.wireOp",EDGE,"E29"),sQuery(id+"F3.wireOp",EDGE,"E30"),sQuery(id+"F3.wireOp",EDGE,"E31"),sQuery(id+"F3.wireOp",EDGE,"E32"),sQuery(id+"F3.wireOp",EDGE,"E33"),sQuery(id+"F3.wireOp",EDGE,"E34"),sQuery(id+"F3.wireOp",EDGE,"E35"),sQuery(id+"F3.wireOp",EDGE,"E36"),sQuery(id+"F3.wireOp",EDGE,"E37"),sQuery(id+"F3.wireOp",EDGE,"E38"),sQuery(id+"F3.wireOp",EDGE,"E39"),sQuery(id+"F3.wireOp",EDGE,"E40"),sQuery(id+"F3.wireOp",EDGE,"E41"),sQuery(id+"F3.wireOp",EDGE,"E42"),sQuery(id+"F3.wireOp",EDGE,"E43"),sQuery(id+"F3.wireOp",EDGE,"E44"),sQuery(id+"F3.wireOp",EDGE,"E45"),sQuery(id+"F3.wireOp",EDGE,"E46"),sQuery(id+"F3.wireOp",EDGE,"E47"),sQuery(id+"F3.wireOp",EDGE,"E48"),sQuery(id+"F3.wireOp",EDGE,"E49"),sQuery(id+"F3.wireOp",EDGE,"E50"),sQuery(id+"F3.wireOp",EDGE,"E51"),sQuery(id+"F3.wireOp",EDGE,"E52"),sQuery(id+"F3.wireOp",EDGE,"E53"),sQuery(id+"F3.wireOp",EDGE,"E54"),sQuery(id+"F3.wireOp",EDGE,"E55"),sQuery(id+"F3.wireOp",EDGE,"E56"),sQuery(id+"F3.wireOp",EDGE,"E57"),sQuery(id+"F3.wireOp",EDGE,"E58"),sQuery(id+"F3.wireOp",EDGE,"E58"),sQuery(id+"F3.wireOp",EDGE,"E59")])]});
            var Q2;
            Q2=makeQuery(id+"F4.opExtrude","SWEPT_BODY",BODY,{"disambiguationData":[OSD([sQuery(id+"F3.wireOp",EDGE,"E60"),sQuery(id+"F3.wireOp",EDGE,"E61"),sQuery(id+"F3.wireOp",EDGE,"E62"),sQuery(id+"F3.wireOp",EDGE,"E63"),sQuery(id+"F3.wireOp",EDGE,"E64"),sQuery(id+"F3.wireOp",EDGE,"E65"),sQuery(id+"F3.wireOp",EDGE,"E66"),sQuery(id+"F3.wireOp",EDGE,"E67"),sQuery(id+"F3.wireOp",EDGE,"E68"),sQuery(id+"F3.wireOp",EDGE,"E69"),sQuery(id+"F3.wireOp",EDGE,"E70"),sQuery(id+"F3.wireOp",EDGE,"E71"),sQuery(id+"F3.wireOp",EDGE,"E72"),sQuery(id+"F3.wireOp",EDGE,"E73"),sQuery(id+"F3.wireOp",EDGE,"E74"),sQuery(id+"F3.wireOp",EDGE,"E75"),sQuery(id+"F3.wireOp",EDGE,"E76"),sQuery(id+"F3.wireOp",EDGE,"E77"),sQuery(id+"F3.wireOp",EDGE,"E78"),sQuery(id+"F3.wireOp",EDGE,"E79"),sQuery(id+"F3.wireOp",EDGE,"E80"),sQuery(id+"F3.wireOp",EDGE,"E81"),sQuery(id+"F3.wireOp",EDGE,"E82"),sQuery(id+"F3.wireOp",EDGE,"E83"),sQuery(id+"F3.wireOp",EDGE,"E84"),sQuery(id+"F3.wireOp",EDGE,"E85"),sQuery(id+"F3.wireOp",EDGE,"E86"),sQuery(id+"F3.wireOp",EDGE,"E87")])]});
            var Q3;
            Q3=makeQuery(id+"F4.opExtrude","SWEPT_BODY",BODY,{"disambiguationData":[OSD([sQuery(id+"F3.wireOp",EDGE,"E88"),sQuery(id+"F3.wireOp",EDGE,"E89"),sQuery(id+"F3.wireOp",EDGE,"E90"),sQuery(id+"F3.wireOp",EDGE,"E91"),sQuery(id+"F3.wireOp",EDGE,"E92"),sQuery(id+"F3.wireOp",EDGE,"E93"),sQuery(id+"F3.wireOp",EDGE,"E94"),sQuery(id+"F3.wireOp",EDGE,"E95"),sQuery(id+"F3.wireOp",EDGE,"E96"),sQuery(id+"F3.wireOp",EDGE,"E97"),sQuery(id+"F3.wireOp",EDGE,"E98"),sQuery(id+"F3.wireOp",EDGE,"E99"),sQuery(id+"F3.wireOp",EDGE,"E100"),sQuery(id+"F3.wireOp",EDGE,"E101"),sQuery(id+"F3.wireOp",EDGE,"E102"),sQuery(id+"F3.wireOp",EDGE,"E103")])]});
            var Q4;
            Q4=makeQuery(id+"F4.opExtrude","SWEPT_BODY",BODY,{"disambiguationData":[OSD([sQuery(id+"F3.wireOp",EDGE,"E104"),sQuery(id+"F3.wireOp",EDGE,"E105"),sQuery(id+"F3.wireOp",EDGE,"E106"),sQuery(id+"F3.wireOp",EDGE,"E107"),sQuery(id+"F3.wireOp",EDGE,"E108"),sQuery(id+"F3.wireOp",EDGE,"E109"),sQuery(id+"F3.wireOp",EDGE,"E110"),sQuery(id+"F3.wireOp",EDGE,"E111")])]});
            var Q5;
            Q5=makeQuery(id+"F4.opExtrude","SWEPT_BODY",BODY,{"disambiguationData":[OSD([sQuery(id+"F3.wireOp",EDGE,"E112"),sQuery(id+"F3.wireOp",EDGE,"E113"),sQuery(id+"F3.wireOp",EDGE,"E114"),sQuery(id+"F3.wireOp",EDGE,"E115"),sQuery(id+"F3.wireOp",EDGE,"E116"),sQuery(id+"F3.wireOp",EDGE,"E117"),sQuery(id+"F3.wireOp",EDGE,"E118"),sQuery(id+"F3.wireOp",EDGE,"E119"),sQuery(id+"F3.wireOp",EDGE,"E120"),sQuery(id+"F3.wireOp",EDGE,"E121"),sQuery(id+"F3.wireOp",EDGE,"E122"),sQuery(id+"F3.wireOp",EDGE,"E123"),sQuery(id+"F3.wireOp",EDGE,"E124"),sQuery(id+"F3.wireOp",EDGE,"E125"),sQuery(id+"F3.wireOp",EDGE,"E126"),sQuery(id+"F3.wireOp",EDGE,"E127"),sQuery(id+"F3.wireOp",EDGE,"E128"),sQuery(id+"F3.wireOp",EDGE,"E129"),sQuery(id+"F3.wireOp",EDGE,"E130"),sQuery(id+"F3.wireOp",EDGE,"E131"),sQuery(id+"F3.wireOp",EDGE,"E132"),sQuery(id+"F3.wireOp",EDGE,"E133"),sQuery(id+"F3.wireOp",EDGE,"E134"),sQuery(id+"F3.wireOp",EDGE,"E135"),sQuery(id+"F3.wireOp",EDGE,"E136"),sQuery(id+"F3.wireOp",EDGE,"E137"),sQuery(id+"F3.wireOp",EDGE,"E138"),sQuery(id+"F3.wireOp",EDGE,"E139"),sQuery(id+"F3.wireOp",EDGE,"E140"),sQuery(id+"F3.wireOp",EDGE,"E141"),sQuery(id+"F3.wireOp",EDGE,"E142"),sQuery(id+"F3.wireOp",EDGE,"E143"),sQuery(id+"F3.wireOp",EDGE,"E144"),sQuery(id+"F3.wireOp",EDGE,"E145"),sQuery(id+"F3.wireOp",EDGE,"E146"),sQuery(id+"F3.wireOp",EDGE,"E147"),sQuery(id+"F3.wireOp",EDGE,"E148"),sQuery(id+"F3.wireOp",EDGE,"E149"),sQuery(id+"F3.wireOp",EDGE,"E150"),sQuery(id+"F3.wireOp",EDGE,"E151"),sQuery(id+"F3.wireOp",EDGE,"E152"),sQuery(id+"F3.wireOp",EDGE,"E153"),sQuery(id+"F3.wireOp",EDGE,"E154"),sQuery(id+"F3.wireOp",EDGE,"E155"),sQuery(id+"F3.wireOp",EDGE,"E156"),sQuery(id+"F3.wireOp",EDGE,"E157"),sQuery(id+"F3.wireOp",EDGE,"E158"),sQuery(id+"F3.wireOp",EDGE,"E159"),sQuery(id+"F3.wireOp",EDGE,"E160"),sQuery(id+"F3.wireOp",EDGE,"E161"),sQuery(id+"F3.wireOp",EDGE,"E162"),sQuery(id+"F3.wireOp",EDGE,"E163"),sQuery(id+"F3.wireOp",EDGE,"E164"),sQuery(id+"F3.wireOp",EDGE,"E165"),sQuery(id+"F3.wireOp",EDGE,"E166"),sQuery(id+"F3.wireOp",EDGE,"E167"),sQuery(id+"F3.wireOp",EDGE,"E168"),sQuery(id+"F3.wireOp",EDGE,"E169"),sQuery(id+"F3.wireOp",EDGE,"E170"),sQuery(id+"F3.wireOp",EDGE,"E171"),sQuery(id+"F3.wireOp",EDGE,"E172"),sQuery(id+"F3.wireOp",EDGE,"E173"),sQuery(id+"F3.wireOp",EDGE,"E174"),sQuery(id+"F3.wireOp",EDGE,"E175"),sQuery(id+"F3.wireOp",EDGE,"E176"),sQuery(id+"F3.wireOp",EDGE,"E177"),sQuery(id+"F3.wireOp",EDGE,"E178"),sQuery(id+"F3.wireOp",EDGE,"E179"),sQuery(id+"F3.wireOp",EDGE,"E180"),sQuery(id+"F3.wireOp",EDGE,"E181"),sQuery(id+"F3.wireOp",EDGE,"E182"),sQuery(id+"F3.wireOp",EDGE,"E183"),sQuery(id+"F3.wireOp",EDGE,"E184"),sQuery(id+"F3.wireOp",EDGE,"E185"),sQuery(id+"F3.wireOp",EDGE,"E186"),sQuery(id+"F3.wireOp",EDGE,"E187"),sQuery(id+"F3.wireOp",EDGE,"E188"),sQuery(id+"F3.wireOp",EDGE,"E189"),sQuery(id+"F3.wireOp",EDGE,"E190"),sQuery(id+"F3.wireOp",EDGE,"E191"),sQuery(id+"F3.wireOp",EDGE,"E192"),sQuery(id+"F3.wireOp",EDGE,"E193"),sQuery(id+"F3.wireOp",EDGE,"E194"),sQuery(id+"F3.wireOp",EDGE,"E195"),sQuery(id+"F3.wireOp",EDGE,"E196"),sQuery(id+"F3.wireOp",EDGE,"E197"),sQuery(id+"F3.wireOp",EDGE,"E198")])]});
            var Q6;
            Q6=makeQuery(id+"F4.opExtrude","SWEPT_BODY",BODY,{"disambiguationData":[OSD([sQuery(id+"F3.wireOp",EDGE,"E199"),sQuery(id+"F3.wireOp",EDGE,"E200"),sQuery(id+"F3.wireOp",EDGE,"E201"),sQuery(id+"F3.wireOp",EDGE,"E202"),sQuery(id+"F3.wireOp",EDGE,"E203"),sQuery(id+"F3.wireOp",EDGE,"E204"),sQuery(id+"F3.wireOp",EDGE,"E205"),sQuery(id+"F3.wireOp",EDGE,"E206"),sQuery(id+"F3.wireOp",EDGE,"E207"),sQuery(id+"F3.wireOp",EDGE,"E208"),sQuery(id+"F3.wireOp",EDGE,"E209"),sQuery(id+"F3.wireOp",EDGE,"E210"),sQuery(id+"F3.wireOp",EDGE,"E211"),sQuery(id+"F3.wireOp",EDGE,"E212"),sQuery(id+"F3.wireOp",EDGE,"E213"),sQuery(id+"F3.wireOp",EDGE,"E214"),sQuery(id+"F3.wireOp",EDGE,"E215"),sQuery(id+"F3.wireOp",EDGE,"E216"),sQuery(id+"F3.wireOp",EDGE,"E217"),sQuery(id+"F3.wireOp",EDGE,"E218"),sQuery(id+"F3.wireOp",EDGE,"E219"),sQuery(id+"F3.wireOp",EDGE,"E220"),sQuery(id+"F3.wireOp",EDGE,"E221"),sQuery(id+"F3.wireOp",EDGE,"E222"),sQuery(id+"F3.wireOp",EDGE,"E223"),sQuery(id+"F3.wireOp",EDGE,"E224"),sQuery(id+"F3.wireOp",EDGE,"E225"),sQuery(id+"F3.wireOp",EDGE,"E226"),sQuery(id+"F3.wireOp",EDGE,"E227")])]});
            var Q7;
            Q7=makeQuery(id+"F4.opExtrude","SWEPT_BODY",BODY,{"disambiguationData":[OSD([sQuery(id+"F3.wireOp",EDGE,"E228"),sQuery(id+"F3.wireOp",EDGE,"E229"),sQuery(id+"F3.wireOp",EDGE,"E230"),sQuery(id+"F3.wireOp",EDGE,"E231"),sQuery(id+"F3.wireOp",EDGE,"E232"),sQuery(id+"F3.wireOp",EDGE,"E233"),sQuery(id+"F3.wireOp",EDGE,"E234"),sQuery(id+"F3.wireOp",EDGE,"E235"),sQuery(id+"F3.wireOp",EDGE,"E236"),sQuery(id+"F3.wireOp",EDGE,"E237"),sQuery(id+"F3.wireOp",EDGE,"E238"),sQuery(id+"F3.wireOp",EDGE,"E239"),sQuery(id+"F3.wireOp",EDGE,"E239"),sQuery(id+"F3.wireOp",EDGE,"E240"),sQuery(id+"F3.wireOp",EDGE,"E241"),sQuery(id+"F3.wireOp",EDGE,"E242"),sQuery(id+"F3.wireOp",EDGE,"E243"),sQuery(id+"F3.wireOp",EDGE,"E244"),sQuery(id+"F3.wireOp",EDGE,"E245"),sQuery(id+"F3.wireOp",EDGE,"E246"),sQuery(id+"F3.wireOp",EDGE,"E247"),sQuery(id+"F3.wireOp",EDGE,"E248"),sQuery(id+"F3.wireOp",EDGE,"E249"),sQuery(id+"F3.wireOp",EDGE,"E250"),sQuery(id+"F3.wireOp",EDGE,"E251"),sQuery(id+"F3.wireOp",EDGE,"E252"),sQuery(id+"F3.wireOp",EDGE,"E253"),sQuery(id+"F3.wireOp",EDGE,"E254"),sQuery(id+"F3.wireOp",EDGE,"E255"),sQuery(id+"F3.wireOp",EDGE,"E256"),sQuery(id+"F3.wireOp",EDGE,"E257"),sQuery(id+"F3.wireOp",EDGE,"E258"),sQuery(id+"F3.wireOp",EDGE,"E259"),sQuery(id+"F3.wireOp",EDGE,"E260")])]});
            var Q8;
            Q8=sQuery(id+"F6.wireOp",EDGE,"E278");
            transform(context, id + "F7", {"entities" : qUnion([Q0, Q1, Q2, Q3, Q4, Q5, Q6, Q7]), "transformType" : TransformType.TRANSLATION_ENTITY, "oppositeDirectionEntity" : false, "transformLine" : qUnion([Q8]), "makeCopy" : false});
        }
        {
            var Q0;
            Q0=makeQuery(id+"F4.opExtrude","SWEPT_BODY",BODY,{"disambiguationData":[OSD([sQuery(id+"F3.wireOp",EDGE,"E88"),sQuery(id+"F3.wireOp",EDGE,"E89"),sQuery(id+"F3.wireOp",EDGE,"E90"),sQuery(id+"F3.wireOp",EDGE,"E91"),sQuery(id+"F3.wireOp",EDGE,"E92"),sQuery(id+"F3.wireOp",EDGE,"E93"),sQuery(id+"F3.wireOp",EDGE,"E94"),sQuery(id+"F3.wireOp",EDGE,"E95"),sQuery(id+"F3.wireOp",EDGE,"E96"),sQuery(id+"F3.wireOp",EDGE,"E97"),sQuery(id+"F3.wireOp",EDGE,"E98"),sQuery(id+"F3.wireOp",EDGE,"E99"),sQuery(id+"F3.wireOp",EDGE,"E100"),sQuery(id+"F3.wireOp",EDGE,"E101"),sQuery(id+"F3.wireOp",EDGE,"E102"),sQuery(id+"F3.wireOp",EDGE,"E103")])]});
            var Q1;
            Q1=makeQuery(id+"F4.opExtrude","SWEPT_BODY",BODY,{"disambiguationData":[OSD([sQuery(id+"F3.wireOp",EDGE,"E104"),sQuery(id+"F3.wireOp",EDGE,"E105"),sQuery(id+"F3.wireOp",EDGE,"E106"),sQuery(id+"F3.wireOp",EDGE,"E107"),sQuery(id+"F3.wireOp",EDGE,"E108"),sQuery(id+"F3.wireOp",EDGE,"E109"),sQuery(id+"F3.wireOp",EDGE,"E110"),sQuery(id+"F3.wireOp",EDGE,"E111")])]});
            var Q2;
            Q2=makeQuery(id+"F4.opExtrude","SWEPT_BODY",BODY,{"disambiguationData":[OSD([sQuery(id+"F3.wireOp",EDGE,"E112"),sQuery(id+"F3.wireOp",EDGE,"E113"),sQuery(id+"F3.wireOp",EDGE,"E114"),sQuery(id+"F3.wireOp",EDGE,"E115"),sQuery(id+"F3.wireOp",EDGE,"E116"),sQuery(id+"F3.wireOp",EDGE,"E117"),sQuery(id+"F3.wireOp",EDGE,"E118"),sQuery(id+"F3.wireOp",EDGE,"E119"),sQuery(id+"F3.wireOp",EDGE,"E120"),sQuery(id+"F3.wireOp",EDGE,"E121"),sQuery(id+"F3.wireOp",EDGE,"E122"),sQuery(id+"F3.wireOp",EDGE,"E123"),sQuery(id+"F3.wireOp",EDGE,"E124"),sQuery(id+"F3.wireOp",EDGE,"E125"),sQuery(id+"F3.wireOp",EDGE,"E126"),sQuery(id+"F3.wireOp",EDGE,"E127"),sQuery(id+"F3.wireOp",EDGE,"E128"),sQuery(id+"F3.wireOp",EDGE,"E129"),sQuery(id+"F3.wireOp",EDGE,"E130"),sQuery(id+"F3.wireOp",EDGE,"E131"),sQuery(id+"F3.wireOp",EDGE,"E132"),sQuery(id+"F3.wireOp",EDGE,"E133"),sQuery(id+"F3.wireOp",EDGE,"E134"),sQuery(id+"F3.wireOp",EDGE,"E135"),sQuery(id+"F3.wireOp",EDGE,"E136"),sQuery(id+"F3.wireOp",EDGE,"E137"),sQuery(id+"F3.wireOp",EDGE,"E138"),sQuery(id+"F3.wireOp",EDGE,"E139"),sQuery(id+"F3.wireOp",EDGE,"E140"),sQuery(id+"F3.wireOp",EDGE,"E141"),sQuery(id+"F3.wireOp",EDGE,"E142"),sQuery(id+"F3.wireOp",EDGE,"E143"),sQuery(id+"F3.wireOp",EDGE,"E144"),sQuery(id+"F3.wireOp",EDGE,"E145"),sQuery(id+"F3.wireOp",EDGE,"E146"),sQuery(id+"F3.wireOp",EDGE,"E147"),sQuery(id+"F3.wireOp",EDGE,"E148"),sQuery(id+"F3.wireOp",EDGE,"E149"),sQuery(id+"F3.wireOp",EDGE,"E150"),sQuery(id+"F3.wireOp",EDGE,"E151"),sQuery(id+"F3.wireOp",EDGE,"E152"),sQuery(id+"F3.wireOp",EDGE,"E153"),sQuery(id+"F3.wireOp",EDGE,"E154"),sQuery(id+"F3.wireOp",EDGE,"E155"),sQuery(id+"F3.wireOp",EDGE,"E156"),sQuery(id+"F3.wireOp",EDGE,"E157"),sQuery(id+"F3.wireOp",EDGE,"E158"),sQuery(id+"F3.wireOp",EDGE,"E159"),sQuery(id+"F3.wireOp",EDGE,"E160"),sQuery(id+"F3.wireOp",EDGE,"E161"),sQuery(id+"F3.wireOp",EDGE,"E162"),sQuery(id+"F3.wireOp",EDGE,"E163"),sQuery(id+"F3.wireOp",EDGE,"E164"),sQuery(id+"F3.wireOp",EDGE,"E165"),sQuery(id+"F3.wireOp",EDGE,"E166"),sQuery(id+"F3.wireOp",EDGE,"E167"),sQuery(id+"F3.wireOp",EDGE,"E168"),sQuery(id+"F3.wireOp",EDGE,"E169"),sQuery(id+"F3.wireOp",EDGE,"E170"),sQuery(id+"F3.wireOp",EDGE,"E171"),sQuery(id+"F3.wireOp",EDGE,"E172"),sQuery(id+"F3.wireOp",EDGE,"E173"),sQuery(id+"F3.wireOp",EDGE,"E174"),sQuery(id+"F3.wireOp",EDGE,"E175"),sQuery(id+"F3.wireOp",EDGE,"E176"),sQuery(id+"F3.wireOp",EDGE,"E177"),sQuery(id+"F3.wireOp",EDGE,"E178"),sQuery(id+"F3.wireOp",EDGE,"E179"),sQuery(id+"F3.wireOp",EDGE,"E180"),sQuery(id+"F3.wireOp",EDGE,"E181"),sQuery(id+"F3.wireOp",EDGE,"E182"),sQuery(id+"F3.wireOp",EDGE,"E183"),sQuery(id+"F3.wireOp",EDGE,"E184"),sQuery(id+"F3.wireOp",EDGE,"E185"),sQuery(id+"F3.wireOp",EDGE,"E186"),sQuery(id+"F3.wireOp",EDGE,"E187"),sQuery(id+"F3.wireOp",EDGE,"E188"),sQuery(id+"F3.wireOp",EDGE,"E189"),sQuery(id+"F3.wireOp",EDGE,"E190"),sQuery(id+"F3.wireOp",EDGE,"E191"),sQuery(id+"F3.wireOp",EDGE,"E192"),sQuery(id+"F3.wireOp",EDGE,"E193"),sQuery(id+"F3.wireOp",EDGE,"E194"),sQuery(id+"F3.wireOp",EDGE,"E195"),sQuery(id+"F3.wireOp",EDGE,"E196"),sQuery(id+"F3.wireOp",EDGE,"E197"),sQuery(id+"F3.wireOp",EDGE,"E198")])]});
            var Q3;
            Q3=makeQuery(id+"F4.opExtrude","SWEPT_BODY",BODY,{"disambiguationData":[OSD([sQuery(id+"F3.wireOp",EDGE,"E199"),sQuery(id+"F3.wireOp",EDGE,"E200"),sQuery(id+"F3.wireOp",EDGE,"E201"),sQuery(id+"F3.wireOp",EDGE,"E202"),sQuery(id+"F3.wireOp",EDGE,"E203"),sQuery(id+"F3.wireOp",EDGE,"E204"),sQuery(id+"F3.wireOp",EDGE,"E205"),sQuery(id+"F3.wireOp",EDGE,"E206"),sQuery(id+"F3.wireOp",EDGE,"E207"),sQuery(id+"F3.wireOp",EDGE,"E208"),sQuery(id+"F3.wireOp",EDGE,"E209"),sQuery(id+"F3.wireOp",EDGE,"E210"),sQuery(id+"F3.wireOp",EDGE,"E211"),sQuery(id+"F3.wireOp",EDGE,"E212"),sQuery(id+"F3.wireOp",EDGE,"E213"),sQuery(id+"F3.wireOp",EDGE,"E214"),sQuery(id+"F3.wireOp",EDGE,"E215"),sQuery(id+"F3.wireOp",EDGE,"E216"),sQuery(id+"F3.wireOp",EDGE,"E217"),sQuery(id+"F3.wireOp",EDGE,"E218"),sQuery(id+"F3.wireOp",EDGE,"E219"),sQuery(id+"F3.wireOp",EDGE,"E220"),sQuery(id+"F3.wireOp",EDGE,"E221"),sQuery(id+"F3.wireOp",EDGE,"E222"),sQuery(id+"F3.wireOp",EDGE,"E223"),sQuery(id+"F3.wireOp",EDGE,"E224"),sQuery(id+"F3.wireOp",EDGE,"E225"),sQuery(id+"F3.wireOp",EDGE,"E226"),sQuery(id+"F3.wireOp",EDGE,"E227")])]});
            var Q4;
            Q4=makeQuery(id+"F4.opExtrude","SWEPT_BODY",BODY,{"disambiguationData":[OSD([sQuery(id+"F3.wireOp",EDGE,"E228"),sQuery(id+"F3.wireOp",EDGE,"E229"),sQuery(id+"F3.wireOp",EDGE,"E230"),sQuery(id+"F3.wireOp",EDGE,"E231"),sQuery(id+"F3.wireOp",EDGE,"E232"),sQuery(id+"F3.wireOp",EDGE,"E233"),sQuery(id+"F3.wireOp",EDGE,"E234"),sQuery(id+"F3.wireOp",EDGE,"E235"),sQuery(id+"F3.wireOp",EDGE,"E236"),sQuery(id+"F3.wireOp",EDGE,"E237"),sQuery(id+"F3.wireOp",EDGE,"E238"),sQuery(id+"F3.wireOp",EDGE,"E239"),sQuery(id+"F3.wireOp",EDGE,"E239"),sQuery(id+"F3.wireOp",EDGE,"E240"),sQuery(id+"F3.wireOp",EDGE,"E241"),sQuery(id+"F3.wireOp",EDGE,"E242"),sQuery(id+"F3.wireOp",EDGE,"E243"),sQuery(id+"F3.wireOp",EDGE,"E244"),sQuery(id+"F3.wireOp",EDGE,"E245"),sQuery(id+"F3.wireOp",EDGE,"E246"),sQuery(id+"F3.wireOp",EDGE,"E247"),sQuery(id+"F3.wireOp",EDGE,"E248"),sQuery(id+"F3.wireOp",EDGE,"E249"),sQuery(id+"F3.wireOp",EDGE,"E250"),sQuery(id+"F3.wireOp",EDGE,"E251"),sQuery(id+"F3.wireOp",EDGE,"E252"),sQuery(id+"F3.wireOp",EDGE,"E253"),sQuery(id+"F3.wireOp",EDGE,"E254"),sQuery(id+"F3.wireOp",EDGE,"E255"),sQuery(id+"F3.wireOp",EDGE,"E256"),sQuery(id+"F3.wireOp",EDGE,"E257"),sQuery(id+"F3.wireOp",EDGE,"E258"),sQuery(id+"F3.wireOp",EDGE,"E259"),sQuery(id+"F3.wireOp",EDGE,"E260")])]});
            var Q5;
            Q5=makeQuery(id+"F4.opExtrude","SWEPT_BODY",BODY,{"disambiguationData":[OSD([sQuery(id+"F3.wireOp",EDGE,"E261"),sQuery(id+"F3.wireOp",EDGE,"E262"),sQuery(id+"F3.wireOp",EDGE,"E263"),sQuery(id+"F3.wireOp",EDGE,"E264"),sQuery(id+"F3.wireOp",EDGE,"E265"),sQuery(id+"F3.wireOp",EDGE,"E266"),sQuery(id+"F3.wireOp",EDGE,"E267"),sQuery(id+"F3.wireOp",EDGE,"E268"),sQuery(id+"F3.wireOp",EDGE,"E269"),sQuery(id+"F3.wireOp",EDGE,"E270"),sQuery(id+"F3.wireOp",EDGE,"E271"),sQuery(id+"F3.wireOp",EDGE,"E272"),sQuery(id+"F3.wireOp",EDGE,"E273"),sQuery(id+"F3.wireOp",EDGE,"E274"),sQuery(id+"F3.wireOp",EDGE,"E275"),sQuery(id+"F3.wireOp",EDGE,"E276")])]});
            deleteBodies(context, id + "F8", {"entities" : qUnion([Q0, Q1, Q2, Q3, Q4, Q5])});
        }
        {
            var Q0;
            Q0=makeQuery(id+"F4.opExtrude","SWEPT_BODY",BODY,{"disambiguationData":[OSD([sQuery(id+"F3.wireOp",EDGE,"E24"),sQuery(id+"F3.wireOp",EDGE,"E25"),sQuery(id+"F3.wireOp",EDGE,"E26"),sQuery(id+"F3.wireOp",EDGE,"E27"),sQuery(id+"F3.wireOp",EDGE,"E28"),sQuery(id+"F3.wireOp",EDGE,"E29"),sQuery(id+"F3.wireOp",EDGE,"E30"),sQuery(id+"F3.wireOp",EDGE,"E31"),sQuery(id+"F3.wireOp",EDGE,"E32"),sQuery(id+"F3.wireOp",EDGE,"E33"),sQuery(id+"F3.wireOp",EDGE,"E34"),sQuery(id+"F3.wireOp",EDGE,"E35"),sQuery(id+"F3.wireOp",EDGE,"E36"),sQuery(id+"F3.wireOp",EDGE,"E37"),sQuery(id+"F3.wireOp",EDGE,"E38"),sQuery(id+"F3.wireOp",EDGE,"E39"),sQuery(id+"F3.wireOp",EDGE,"E40"),sQuery(id+"F3.wireOp",EDGE,"E41"),sQuery(id+"F3.wireOp",EDGE,"E42"),sQuery(id+"F3.wireOp",EDGE,"E43"),sQuery(id+"F3.wireOp",EDGE,"E44"),sQuery(id+"F3.wireOp",EDGE,"E45"),sQuery(id+"F3.wireOp",EDGE,"E46"),sQuery(id+"F3.wireOp",EDGE,"E47"),sQuery(id+"F3.wireOp",EDGE,"E48"),sQuery(id+"F3.wireOp",EDGE,"E49"),sQuery(id+"F3.wireOp",EDGE,"E50"),sQuery(id+"F3.wireOp",EDGE,"E51"),sQuery(id+"F3.wireOp",EDGE,"E52"),sQuery(id+"F3.wireOp",EDGE,"E53"),sQuery(id+"F3.wireOp",EDGE,"E54"),sQuery(id+"F3.wireOp",EDGE,"E55"),sQuery(id+"F3.wireOp",EDGE,"E56"),sQuery(id+"F3.wireOp",EDGE,"E57"),sQuery(id+"F3.wireOp",EDGE,"E58"),sQuery(id+"F3.wireOp",EDGE,"E58"),sQuery(id+"F3.wireOp",EDGE,"E59")])]});
            var Q1;
            Q1=makeQuery(id+"F4.opExtrude","SWEPT_BODY",BODY,{"disambiguationData":[OSD([sQuery(id+"F3.wireOp",EDGE,"E60"),sQuery(id+"F3.wireOp",EDGE,"E61"),sQuery(id+"F3.wireOp",EDGE,"E62"),sQuery(id+"F3.wireOp",EDGE,"E63"),sQuery(id+"F3.wireOp",EDGE,"E64"),sQuery(id+"F3.wireOp",EDGE,"E65"),sQuery(id+"F3.wireOp",EDGE,"E66"),sQuery(id+"F3.wireOp",EDGE,"E67"),sQuery(id+"F3.wireOp",EDGE,"E68"),sQuery(id+"F3.wireOp",EDGE,"E69"),sQuery(id+"F3.wireOp",EDGE,"E70"),sQuery(id+"F3.wireOp",EDGE,"E71"),sQuery(id+"F3.wireOp",EDGE,"E72"),sQuery(id+"F3.wireOp",EDGE,"E73"),sQuery(id+"F3.wireOp",EDGE,"E74"),sQuery(id+"F3.wireOp",EDGE,"E75"),sQuery(id+"F3.wireOp",EDGE,"E76"),sQuery(id+"F3.wireOp",EDGE,"E77"),sQuery(id+"F3.wireOp",EDGE,"E78"),sQuery(id+"F3.wireOp",EDGE,"E79"),sQuery(id+"F3.wireOp",EDGE,"E80"),sQuery(id+"F3.wireOp",EDGE,"E81"),sQuery(id+"F3.wireOp",EDGE,"E82"),sQuery(id+"F3.wireOp",EDGE,"E83"),sQuery(id+"F3.wireOp",EDGE,"E84"),sQuery(id+"F3.wireOp",EDGE,"E85"),sQuery(id+"F3.wireOp",EDGE,"E86"),sQuery(id+"F3.wireOp",EDGE,"E87")])]});
            var Q2;
            Q2=makeQuery(id+"F4.opExtrude","CAP_VERTEX",VERTEX,{"disambiguationData":[OSD([sQuery(id+"F3.wireOp",EDGE,"E81"),sQuery(id+"F3.wireOp",EDGE,"E82")])],"isStart":true});
            transform(context, id + "F9", {"entities" : qUnion([Q0, Q1]), "transformType" : TransformType.SCALE_UNIFORMLY, "scale" : 2.6, "scalePoint" : qUnion([Q2]), "makeCopy" : false});
        }
        {
            var Q0;
            Q0=makeQuery(id+"F4.opExtrude","SWEPT_BODY",BODY,{"disambiguationData":[OSD([sQuery(id+"F3.wireOp",EDGE,"E24"),sQuery(id+"F3.wireOp",EDGE,"E25"),sQuery(id+"F3.wireOp",EDGE,"E26"),sQuery(id+"F3.wireOp",EDGE,"E27"),sQuery(id+"F3.wireOp",EDGE,"E28"),sQuery(id+"F3.wireOp",EDGE,"E29"),sQuery(id+"F3.wireOp",EDGE,"E30"),sQuery(id+"F3.wireOp",EDGE,"E31"),sQuery(id+"F3.wireOp",EDGE,"E32"),sQuery(id+"F3.wireOp",EDGE,"E33"),sQuery(id+"F3.wireOp",EDGE,"E34"),sQuery(id+"F3.wireOp",EDGE,"E35"),sQuery(id+"F3.wireOp",EDGE,"E36"),sQuery(id+"F3.wireOp",EDGE,"E37"),sQuery(id+"F3.wireOp",EDGE,"E38"),sQuery(id+"F3.wireOp",EDGE,"E39"),sQuery(id+"F3.wireOp",EDGE,"E40"),sQuery(id+"F3.wireOp",EDGE,"E41"),sQuery(id+"F3.wireOp",EDGE,"E42"),sQuery(id+"F3.wireOp",EDGE,"E43"),sQuery(id+"F3.wireOp",EDGE,"E44"),sQuery(id+"F3.wireOp",EDGE,"E45"),sQuery(id+"F3.wireOp",EDGE,"E46"),sQuery(id+"F3.wireOp",EDGE,"E47"),sQuery(id+"F3.wireOp",EDGE,"E48"),sQuery(id+"F3.wireOp",EDGE,"E49"),sQuery(id+"F3.wireOp",EDGE,"E50"),sQuery(id+"F3.wireOp",EDGE,"E51"),sQuery(id+"F3.wireOp",EDGE,"E52"),sQuery(id+"F3.wireOp",EDGE,"E53"),sQuery(id+"F3.wireOp",EDGE,"E54"),sQuery(id+"F3.wireOp",EDGE,"E55"),sQuery(id+"F3.wireOp",EDGE,"E56"),sQuery(id+"F3.wireOp",EDGE,"E57"),sQuery(id+"F3.wireOp",EDGE,"E58"),sQuery(id+"F3.wireOp",EDGE,"E58"),sQuery(id+"F3.wireOp",EDGE,"E59")])]});
            var Q1;
            Q1=makeQuery(id+"F4.opExtrude","SWEPT_BODY",BODY,{"disambiguationData":[OSD([sQuery(id+"F3.wireOp",EDGE,"E60"),sQuery(id+"F3.wireOp",EDGE,"E61"),sQuery(id+"F3.wireOp",EDGE,"E62"),sQuery(id+"F3.wireOp",EDGE,"E63"),sQuery(id+"F3.wireOp",EDGE,"E64"),sQuery(id+"F3.wireOp",EDGE,"E65"),sQuery(id+"F3.wireOp",EDGE,"E66"),sQuery(id+"F3.wireOp",EDGE,"E67"),sQuery(id+"F3.wireOp",EDGE,"E68"),sQuery(id+"F3.wireOp",EDGE,"E69"),sQuery(id+"F3.wireOp",EDGE,"E70"),sQuery(id+"F3.wireOp",EDGE,"E71"),sQuery(id+"F3.wireOp",EDGE,"E72"),sQuery(id+"F3.wireOp",EDGE,"E73"),sQuery(id+"F3.wireOp",EDGE,"E74"),sQuery(id+"F3.wireOp",EDGE,"E75"),sQuery(id+"F3.wireOp",EDGE,"E76"),sQuery(id+"F3.wireOp",EDGE,"E77"),sQuery(id+"F3.wireOp",EDGE,"E78"),sQuery(id+"F3.wireOp",EDGE,"E79"),sQuery(id+"F3.wireOp",EDGE,"E80"),sQuery(id+"F3.wireOp",EDGE,"E81"),sQuery(id+"F3.wireOp",EDGE,"E82"),sQuery(id+"F3.wireOp",EDGE,"E83"),sQuery(id+"F3.wireOp",EDGE,"E84"),sQuery(id+"F3.wireOp",EDGE,"E85"),sQuery(id+"F3.wireOp",EDGE,"E86"),sQuery(id+"F3.wireOp",EDGE,"E87")])]});
            transform(context, id + "F10", {"entities" : qUnion([Q0, Q1]), "transformType" : TransformType.TRANSLATION_3D, "dx" : 17.7 * mm, "dy" : 0.5 * mm, "dz" : -8.5 * mm, "makeCopy" : false});
        }
        {
            var Q0;
            Q0=makeQuery(id+"F4.opExtrude","SWEPT_BODY",BODY,{"disambiguationData":[OSD([sQuery(id+"F3.wireOp",EDGE,"E60"),sQuery(id+"F3.wireOp",EDGE,"E61"),sQuery(id+"F3.wireOp",EDGE,"E62"),sQuery(id+"F3.wireOp",EDGE,"E63"),sQuery(id+"F3.wireOp",EDGE,"E64"),sQuery(id+"F3.wireOp",EDGE,"E65"),sQuery(id+"F3.wireOp",EDGE,"E66"),sQuery(id+"F3.wireOp",EDGE,"E67"),sQuery(id+"F3.wireOp",EDGE,"E68"),sQuery(id+"F3.wireOp",EDGE,"E69"),sQuery(id+"F3.wireOp",EDGE,"E70"),sQuery(id+"F3.wireOp",EDGE,"E71"),sQuery(id+"F3.wireOp",EDGE,"E72"),sQuery(id+"F3.wireOp",EDGE,"E73"),sQuery(id+"F3.wireOp",EDGE,"E74"),sQuery(id+"F3.wireOp",EDGE,"E75"),sQuery(id+"F3.wireOp",EDGE,"E76"),sQuery(id+"F3.wireOp",EDGE,"E77"),sQuery(id+"F3.wireOp",EDGE,"E78"),sQuery(id+"F3.wireOp",EDGE,"E79"),sQuery(id+"F3.wireOp",EDGE,"E80"),sQuery(id+"F3.wireOp",EDGE,"E81"),sQuery(id+"F3.wireOp",EDGE,"E82"),sQuery(id+"F3.wireOp",EDGE,"E83"),sQuery(id+"F3.wireOp",EDGE,"E84"),sQuery(id+"F3.wireOp",EDGE,"E85"),sQuery(id+"F3.wireOp",EDGE,"E86"),sQuery(id+"F3.wireOp",EDGE,"E87")])]});
            var Q1;
            Q1=makeQuery(id+"F4.opExtrude","SWEPT_BODY",BODY,{"disambiguationData":[OSD([sQuery(id+"F3.wireOp",EDGE,"E24"),sQuery(id+"F3.wireOp",EDGE,"E25"),sQuery(id+"F3.wireOp",EDGE,"E26"),sQuery(id+"F3.wireOp",EDGE,"E27"),sQuery(id+"F3.wireOp",EDGE,"E28"),sQuery(id+"F3.wireOp",EDGE,"E29"),sQuery(id+"F3.wireOp",EDGE,"E30"),sQuery(id+"F3.wireOp",EDGE,"E31"),sQuery(id+"F3.wireOp",EDGE,"E32"),sQuery(id+"F3.wireOp",EDGE,"E33"),sQuery(id+"F3.wireOp",EDGE,"E34"),sQuery(id+"F3.wireOp",EDGE,"E35"),sQuery(id+"F3.wireOp",EDGE,"E36"),sQuery(id+"F3.wireOp",EDGE,"E37"),sQuery(id+"F3.wireOp",EDGE,"E38"),sQuery(id+"F3.wireOp",EDGE,"E39"),sQuery(id+"F3.wireOp",EDGE,"E40"),sQuery(id+"F3.wireOp",EDGE,"E41"),sQuery(id+"F3.wireOp",EDGE,"E42"),sQuery(id+"F3.wireOp",EDGE,"E43"),sQuery(id+"F3.wireOp",EDGE,"E44"),sQuery(id+"F3.wireOp",EDGE,"E45"),sQuery(id+"F3.wireOp",EDGE,"E46"),sQuery(id+"F3.wireOp",EDGE,"E47"),sQuery(id+"F3.wireOp",EDGE,"E48"),sQuery(id+"F3.wireOp",EDGE,"E49"),sQuery(id+"F3.wireOp",EDGE,"E50"),sQuery(id+"F3.wireOp",EDGE,"E51"),sQuery(id+"F3.wireOp",EDGE,"E52"),sQuery(id+"F3.wireOp",EDGE,"E53"),sQuery(id+"F3.wireOp",EDGE,"E54"),sQuery(id+"F3.wireOp",EDGE,"E55"),sQuery(id+"F3.wireOp",EDGE,"E56"),sQuery(id+"F3.wireOp",EDGE,"E57"),sQuery(id+"F3.wireOp",EDGE,"E58"),sQuery(id+"F3.wireOp",EDGE,"E58"),sQuery(id+"F3.wireOp",EDGE,"E59")])]});
            var Q2;
            Q2=makeQuery(id+"F1.opExtrude","SWEPT_BODY",BODY,{"disambiguationData":[OSD([sQuery(id+"F0.wireOp",EDGE,"E0"),sQuery(id+"F0.wireOp",EDGE,"E1"),sQuery(id+"F0.wireOp",EDGE,"E3"),sQuery(id+"F0.wireOp",EDGE,"E4"),sQuery(id+"F0.wireOp",EDGE,"E5"),sQuery(id+"F0.wireOp",EDGE,"E6"),sQuery(id+"F0.wireOp",EDGE,"E7.MirrorCS"),sQuery(id+"F0.wireOp",EDGE,"E8.MirrorCS"),sQuery(id+"F0.wireOp",EDGE,"E9.MirrorCS"),sQuery(id+"F0.wireOp",EDGE,"e2a2dabb-557d-459b-9b9f-5adb2272a29e0.MirrorCS"),sQuery(id+"F0.wireOp",EDGE,"E10.MirrorCS"),sQuery(id+"F0.wireOp",EDGE,"E11.MirrorCS"),sQuery(id+"F0.wireOp",EDGE,"707140a6-f7ec-4781-8bc6-803652c13a771"),sQuery(id+"F0.wireOp",EDGE,"49fe3cd1-9238-4b7c-a740-6a605a94457d1"),sQuery(id+"F0.wireOp",EDGE,"E14.trimOffspring")])]});
            booleanBodies(context, id + "F11", {"operationType" : BooleanOperationType.SUBTRACTION, "tools" : qUnion([Q0, Q1]), "targets" : qUnion([Q2])});
        }
        {
            var Q0;
            Q0=makeQuery(id+"F1.opExtrude","SWEPT_FACE",FACE,{"disambiguationData":[OSD([sQuery(id+"F0.wireOp",EDGE,"E4")])]});
            var sketch = newSketch(context, id + "F12", { "sketchPlane" : qUnion([Q0])});
            skLineSegment(sketch, "E279", {"start": v(-18.78, 25) * mm, "end": v(1.45, 0) * mm, "construction": true});
            skPoint(sketch, "E280", {"position": v(-8.66, 12.5) * mm});
            skLineSegment(sketch, "E281", {"start": v(-8.66, 25) * mm, "end": v(-8.66, 12.5) * mm, "construction": true});
            skLineSegment(sketch, "E282", {"start": v(-8.66, 12.5) * mm, "end": v(-8.66, 0) * mm, "construction": true});
            skPoint(sketch, "E283", {"position": v(-8.66, 18.75) * mm});
            skPoint(sketch, "E284", {"position": v(-8.66, 6.25) * mm});
            skSolve(sketch);
        }
        {
            var Q0;
            Q0=sQuery(id+"F12.wireOp",VERTEX,"E283");
            var Q1;
            Q1=sQuery(id+"F12.wireOp",VERTEX,"E284");
            var Q2;
            Q2=makeQuery(id+"F1.opExtrude","SWEPT_BODY",BODY,{"disambiguationData":[OSD([sQuery(id+"F0.wireOp",EDGE,"E0"),sQuery(id+"F0.wireOp",EDGE,"E1"),sQuery(id+"F0.wireOp",EDGE,"E3"),sQuery(id+"F0.wireOp",EDGE,"E4"),sQuery(id+"F0.wireOp",EDGE,"E5"),sQuery(id+"F0.wireOp",EDGE,"E6"),sQuery(id+"F0.wireOp",EDGE,"E7.MirrorCS"),sQuery(id+"F0.wireOp",EDGE,"E8.MirrorCS"),sQuery(id+"F0.wireOp",EDGE,"E9.MirrorCS"),sQuery(id+"F0.wireOp",EDGE,"E10.MirrorCS"),sQuery(id+"F0.wireOp",EDGE,"E11.MirrorCS"),sQuery(id+"F0.wireOp",EDGE,"E14.trimOffspring"),sQuery(id+"F0.wireOp",EDGE,"E17"),sQuery(id+"F0.wireOp",EDGE,"E18"),sQuery(id+"F0.wireOp",EDGE,"E19"),sQuery(id+"F0.wireOp",EDGE,"E20"),sQuery(id+"F0.wireOp",EDGE,"E21"),sQuery(id+"F0.wireOp",EDGE,"E22"),sQuery(id+"F0.wireOp",EDGE,"E23")])]});
            hole(context, id + "F13", {"style" : HoleStyle.SIMPLE, "endStyle" : HoleEndStyle.BLIND, "standardTappedOrClearance" : lookupTablePath({ "standard" : "ISO", "engagement" : "75%", "pitch" : "0.8 mm", "size" : "M5", "type" : "Tapped" }), "standardBlindInLast" : lookupTablePath({ "standard" : "ISO", "fit" : "Normal", "engagement" : "75%", "pitch" : "0.8 mm", "size" : "M5", "type" : "Clearance & tapped" }), "holeDiameter" : 4.2 * mm, "majorDiameter" : 5 * mm, "showTappedDepth" : true, "holeDepth" : 14.4 * mm, "isTappedThrough" : true, "tappedDepth" : 12 * mm, "tapClearance" : 3, "locations" : qUnion([Q0, Q1]), "scope" : qUnion([Q2])});
        }
        {
            var Q0;
            Q0=makeQuery(id+"F1.opExtrude","CAP_EDGE",EDGE,{"disambiguationData":[OSD([sQuery(id+"F0.wireOp",EDGE,"E23")])],"isStart":false});
            var Q1;
            Q1=makeQuery(id+"F1.opExtrude","CAP_EDGE",EDGE,{"disambiguationData":[OSD([sQuery(id+"F0.wireOp",EDGE,"E17")])],"isStart":false});
            var Q2;
            Q2=makeQuery(id+"F1.opExtrude","CAP_EDGE",EDGE,{"disambiguationData":[OSD([sQuery(id+"F0.wireOp",EDGE,"E22")])],"isStart":false});
            var Q3;
            {var subQ0=sQuery(id+"F0.wireOp",EDGE,"E23");var subQ1=sQuery(id+"F0.wireOp",EDGE,"E22");Q3=makeQuery(id+"F2.opFillet","BLEND_EDGE",EDGE,{"blendedFrom":[makeQuery(id+"F1.opExtrude","SWEPT_EDGE",EDGE,{"disambiguationData":[OSD([subQ1,subQ0])]}),makeQuery(id+"F1.opExtrude","CAP_FACE",FACE,{"disambiguationData":[OSD([sQuery(id+"F0.wireOp",EDGE,"E0"),sQuery(id+"F0.wireOp",EDGE,"E1"),sQuery(id+"F0.wireOp",EDGE,"E3"),sQuery(id+"F0.wireOp",EDGE,"E4"),sQuery(id+"F0.wireOp",EDGE,"E5"),sQuery(id+"F0.wireOp",EDGE,"E6"),sQuery(id+"F0.wireOp",EDGE,"E7.MirrorCS"),sQuery(id+"F0.wireOp",EDGE,"E8.MirrorCS"),sQuery(id+"F0.wireOp",EDGE,"E9.MirrorCS"),sQuery(id+"F0.wireOp",EDGE,"E10.MirrorCS"),sQuery(id+"F0.wireOp",EDGE,"E11.MirrorCS"),sQuery(id+"F0.wireOp",EDGE,"E14.trimOffspring"),sQuery(id+"F0.wireOp",EDGE,"E17"),sQuery(id+"F0.wireOp",EDGE,"E18"),sQuery(id+"F0.wireOp",EDGE,"E19"),sQuery(id+"F0.wireOp",EDGE,"E20"),sQuery(id+"F0.wireOp",EDGE,"E21"),subQ1,subQ0])],"isStart":false})],"blendedInto":[makeQuery(id+"F1.opExtrude","CAP_FACE",FACE,{"disambiguationData":[OSD([sQuery(id+"F0.wireOp",EDGE,"E0"),sQuery(id+"F0.wireOp",EDGE,"E1"),sQuery(id+"F0.wireOp",EDGE,"E3"),sQuery(id+"F0.wireOp",EDGE,"E4"),sQuery(id+"F0.wireOp",EDGE,"E5"),sQuery(id+"F0.wireOp",EDGE,"E6"),sQuery(id+"F0.wireOp",EDGE,"E7.MirrorCS"),sQuery(id+"F0.wireOp",EDGE,"E8.MirrorCS"),sQuery(id+"F0.wireOp",EDGE,"E9.MirrorCS"),sQuery(id+"F0.wireOp",EDGE,"E10.MirrorCS"),sQuery(id+"F0.wireOp",EDGE,"E11.MirrorCS"),sQuery(id+"F0.wireOp",EDGE,"E14.trimOffspring"),sQuery(id+"F0.wireOp",EDGE,"E17"),sQuery(id+"F0.wireOp",EDGE,"E18"),sQuery(id+"F0.wireOp",EDGE,"E19"),sQuery(id+"F0.wireOp",EDGE,"E20"),sQuery(id+"F0.wireOp",EDGE,"E21"),subQ1,subQ0])],"isStart":false})]});}
            var Q4;
            {var subQ0=sQuery(id+"F0.wireOp",EDGE,"E23");var subQ1=sQuery(id+"F0.wireOp",EDGE,"E17");Q4=makeQuery(id+"F2.opFillet","BLEND_EDGE",EDGE,{"blendedFrom":[makeQuery(id+"F1.opExtrude","SWEPT_EDGE",EDGE,{"disambiguationData":[OSD([subQ1,subQ0])]}),makeQuery(id+"F1.opExtrude","CAP_FACE",FACE,{"disambiguationData":[OSD([sQuery(id+"F0.wireOp",EDGE,"E0"),sQuery(id+"F0.wireOp",EDGE,"E1"),sQuery(id+"F0.wireOp",EDGE,"E3"),sQuery(id+"F0.wireOp",EDGE,"E4"),sQuery(id+"F0.wireOp",EDGE,"E5"),sQuery(id+"F0.wireOp",EDGE,"E6"),sQuery(id+"F0.wireOp",EDGE,"E7.MirrorCS"),sQuery(id+"F0.wireOp",EDGE,"E8.MirrorCS"),sQuery(id+"F0.wireOp",EDGE,"E9.MirrorCS"),sQuery(id+"F0.wireOp",EDGE,"E10.MirrorCS"),sQuery(id+"F0.wireOp",EDGE,"E11.MirrorCS"),sQuery(id+"F0.wireOp",EDGE,"E14.trimOffspring"),subQ1,sQuery(id+"F0.wireOp",EDGE,"E18"),sQuery(id+"F0.wireOp",EDGE,"E19"),sQuery(id+"F0.wireOp",EDGE,"E20"),sQuery(id+"F0.wireOp",EDGE,"E21"),sQuery(id+"F0.wireOp",EDGE,"E22"),subQ0])],"isStart":false})],"blendedInto":[makeQuery(id+"F1.opExtrude","CAP_FACE",FACE,{"disambiguationData":[OSD([sQuery(id+"F0.wireOp",EDGE,"E0"),sQuery(id+"F0.wireOp",EDGE,"E1"),sQuery(id+"F0.wireOp",EDGE,"E3"),sQuery(id+"F0.wireOp",EDGE,"E4"),sQuery(id+"F0.wireOp",EDGE,"E5"),sQuery(id+"F0.wireOp",EDGE,"E6"),sQuery(id+"F0.wireOp",EDGE,"E7.MirrorCS"),sQuery(id+"F0.wireOp",EDGE,"E8.MirrorCS"),sQuery(id+"F0.wireOp",EDGE,"E9.MirrorCS"),sQuery(id+"F0.wireOp",EDGE,"E10.MirrorCS"),sQuery(id+"F0.wireOp",EDGE,"E11.MirrorCS"),sQuery(id+"F0.wireOp",EDGE,"E14.trimOffspring"),subQ1,sQuery(id+"F0.wireOp",EDGE,"E18"),sQuery(id+"F0.wireOp",EDGE,"E19"),sQuery(id+"F0.wireOp",EDGE,"E20"),sQuery(id+"F0.wireOp",EDGE,"E21"),sQuery(id+"F0.wireOp",EDGE,"E22"),subQ0])],"isStart":false})]});}
            var Q5;
            Q5=makeQuery(id+"F1.opExtrude","CAP_EDGE",EDGE,{"disambiguationData":[OSD([sQuery(id+"F0.wireOp",EDGE,"E21")])],"isStart":false});
            var Q6;
            {var subQ0=sQuery(id+"F0.wireOp",EDGE,"E21");var subQ1=sQuery(id+"F0.wireOp",EDGE,"E17");Q6=makeQuery(id+"F2.opFillet","BLEND_EDGE",EDGE,{"blendedFrom":[makeQuery(id+"F1.opExtrude","SWEPT_EDGE",EDGE,{"disambiguationData":[OSD([subQ1,subQ0])]}),makeQuery(id+"F1.opExtrude","CAP_FACE",FACE,{"disambiguationData":[OSD([sQuery(id+"F0.wireOp",EDGE,"E0"),sQuery(id+"F0.wireOp",EDGE,"E1"),sQuery(id+"F0.wireOp",EDGE,"E3"),sQuery(id+"F0.wireOp",EDGE,"E4"),sQuery(id+"F0.wireOp",EDGE,"E5"),sQuery(id+"F0.wireOp",EDGE,"E6"),sQuery(id+"F0.wireOp",EDGE,"E7.MirrorCS"),sQuery(id+"F0.wireOp",EDGE,"E8.MirrorCS"),sQuery(id+"F0.wireOp",EDGE,"E9.MirrorCS"),sQuery(id+"F0.wireOp",EDGE,"E10.MirrorCS"),sQuery(id+"F0.wireOp",EDGE,"E11.MirrorCS"),sQuery(id+"F0.wireOp",EDGE,"E14.trimOffspring"),subQ1,sQuery(id+"F0.wireOp",EDGE,"E18"),sQuery(id+"F0.wireOp",EDGE,"E19"),sQuery(id+"F0.wireOp",EDGE,"E20"),subQ0,sQuery(id+"F0.wireOp",EDGE,"E22"),sQuery(id+"F0.wireOp",EDGE,"E23")])],"isStart":false})],"blendedInto":[makeQuery(id+"F1.opExtrude","CAP_FACE",FACE,{"disambiguationData":[OSD([sQuery(id+"F0.wireOp",EDGE,"E0"),sQuery(id+"F0.wireOp",EDGE,"E1"),sQuery(id+"F0.wireOp",EDGE,"E3"),sQuery(id+"F0.wireOp",EDGE,"E4"),sQuery(id+"F0.wireOp",EDGE,"E5"),sQuery(id+"F0.wireOp",EDGE,"E6"),sQuery(id+"F0.wireOp",EDGE,"E7.MirrorCS"),sQuery(id+"F0.wireOp",EDGE,"E8.MirrorCS"),sQuery(id+"F0.wireOp",EDGE,"E9.MirrorCS"),sQuery(id+"F0.wireOp",EDGE,"E10.MirrorCS"),sQuery(id+"F0.wireOp",EDGE,"E11.MirrorCS"),sQuery(id+"F0.wireOp",EDGE,"E14.trimOffspring"),subQ1,sQuery(id+"F0.wireOp",EDGE,"E18"),sQuery(id+"F0.wireOp",EDGE,"E19"),sQuery(id+"F0.wireOp",EDGE,"E20"),subQ0,sQuery(id+"F0.wireOp",EDGE,"E22"),sQuery(id+"F0.wireOp",EDGE,"E23")])],"isStart":false})]});}
            var Q7;
            {var subQ0=sQuery(id+"F0.wireOp",EDGE,"E22");var subQ1=sQuery(id+"F0.wireOp",EDGE,"E21");Q7=makeQuery(id+"F2.opFillet","BLEND_EDGE",EDGE,{"blendedFrom":[makeQuery(id+"F1.opExtrude","SWEPT_EDGE",EDGE,{"disambiguationData":[OSD([subQ1,subQ0])]}),makeQuery(id+"F1.opExtrude","CAP_FACE",FACE,{"disambiguationData":[OSD([sQuery(id+"F0.wireOp",EDGE,"E0"),sQuery(id+"F0.wireOp",EDGE,"E1"),sQuery(id+"F0.wireOp",EDGE,"E3"),sQuery(id+"F0.wireOp",EDGE,"E4"),sQuery(id+"F0.wireOp",EDGE,"E5"),sQuery(id+"F0.wireOp",EDGE,"E6"),sQuery(id+"F0.wireOp",EDGE,"E7.MirrorCS"),sQuery(id+"F0.wireOp",EDGE,"E8.MirrorCS"),sQuery(id+"F0.wireOp",EDGE,"E9.MirrorCS"),sQuery(id+"F0.wireOp",EDGE,"E10.MirrorCS"),sQuery(id+"F0.wireOp",EDGE,"E11.MirrorCS"),sQuery(id+"F0.wireOp",EDGE,"E14.trimOffspring"),sQuery(id+"F0.wireOp",EDGE,"E17"),sQuery(id+"F0.wireOp",EDGE,"E18"),sQuery(id+"F0.wireOp",EDGE,"E19"),sQuery(id+"F0.wireOp",EDGE,"E20"),subQ1,subQ0,sQuery(id+"F0.wireOp",EDGE,"E23")])],"isStart":false})],"blendedInto":[makeQuery(id+"F1.opExtrude","CAP_FACE",FACE,{"disambiguationData":[OSD([sQuery(id+"F0.wireOp",EDGE,"E0"),sQuery(id+"F0.wireOp",EDGE,"E1"),sQuery(id+"F0.wireOp",EDGE,"E3"),sQuery(id+"F0.wireOp",EDGE,"E4"),sQuery(id+"F0.wireOp",EDGE,"E5"),sQuery(id+"F0.wireOp",EDGE,"E6"),sQuery(id+"F0.wireOp",EDGE,"E7.MirrorCS"),sQuery(id+"F0.wireOp",EDGE,"E8.MirrorCS"),sQuery(id+"F0.wireOp",EDGE,"E9.MirrorCS"),sQuery(id+"F0.wireOp",EDGE,"E10.MirrorCS"),sQuery(id+"F0.wireOp",EDGE,"E11.MirrorCS"),sQuery(id+"F0.wireOp",EDGE,"E14.trimOffspring"),sQuery(id+"F0.wireOp",EDGE,"E17"),sQuery(id+"F0.wireOp",EDGE,"E18"),sQuery(id+"F0.wireOp",EDGE,"E19"),sQuery(id+"F0.wireOp",EDGE,"E20"),subQ1,subQ0,sQuery(id+"F0.wireOp",EDGE,"E23")])],"isStart":false})]});}
            var Q8;
            Q8=makeQuery(id+"F1.opExtrude","CAP_EDGE",EDGE,{"disambiguationData":[OSD([sQuery(id+"F0.wireOp",EDGE,"E21")])],"isStart":true});
            var Q9;
            {var subQ0=sQuery(id+"F0.wireOp",EDGE,"E22");var subQ1=sQuery(id+"F0.wireOp",EDGE,"E21");Q9=makeQuery(id+"F2.opFillet","BLEND_EDGE",EDGE,{"blendedFrom":[makeQuery(id+"F1.opExtrude","SWEPT_EDGE",EDGE,{"disambiguationData":[OSD([subQ1,subQ0])]}),makeQuery(id+"F1.opExtrude","CAP_FACE",FACE,{"disambiguationData":[OSD([sQuery(id+"F0.wireOp",EDGE,"E0"),sQuery(id+"F0.wireOp",EDGE,"E1"),sQuery(id+"F0.wireOp",EDGE,"E3"),sQuery(id+"F0.wireOp",EDGE,"E4"),sQuery(id+"F0.wireOp",EDGE,"E5"),sQuery(id+"F0.wireOp",EDGE,"E6"),sQuery(id+"F0.wireOp",EDGE,"E7.MirrorCS"),sQuery(id+"F0.wireOp",EDGE,"E8.MirrorCS"),sQuery(id+"F0.wireOp",EDGE,"E9.MirrorCS"),sQuery(id+"F0.wireOp",EDGE,"E10.MirrorCS"),sQuery(id+"F0.wireOp",EDGE,"E11.MirrorCS"),sQuery(id+"F0.wireOp",EDGE,"E14.trimOffspring"),sQuery(id+"F0.wireOp",EDGE,"E17"),sQuery(id+"F0.wireOp",EDGE,"E18"),sQuery(id+"F0.wireOp",EDGE,"E19"),sQuery(id+"F0.wireOp",EDGE,"E20"),subQ1,subQ0,sQuery(id+"F0.wireOp",EDGE,"E23")])],"isStart":true})],"blendedInto":[makeQuery(id+"F1.opExtrude","CAP_FACE",FACE,{"disambiguationData":[OSD([sQuery(id+"F0.wireOp",EDGE,"E0"),sQuery(id+"F0.wireOp",EDGE,"E1"),sQuery(id+"F0.wireOp",EDGE,"E3"),sQuery(id+"F0.wireOp",EDGE,"E4"),sQuery(id+"F0.wireOp",EDGE,"E5"),sQuery(id+"F0.wireOp",EDGE,"E6"),sQuery(id+"F0.wireOp",EDGE,"E7.MirrorCS"),sQuery(id+"F0.wireOp",EDGE,"E8.MirrorCS"),sQuery(id+"F0.wireOp",EDGE,"E9.MirrorCS"),sQuery(id+"F0.wireOp",EDGE,"E10.MirrorCS"),sQuery(id+"F0.wireOp",EDGE,"E11.MirrorCS"),sQuery(id+"F0.wireOp",EDGE,"E14.trimOffspring"),sQuery(id+"F0.wireOp",EDGE,"E17"),sQuery(id+"F0.wireOp",EDGE,"E18"),sQuery(id+"F0.wireOp",EDGE,"E19"),sQuery(id+"F0.wireOp",EDGE,"E20"),subQ1,subQ0,sQuery(id+"F0.wireOp",EDGE,"E23")])],"isStart":true})]});}
            var Q10;
            Q10=makeQuery(id+"F1.opExtrude","CAP_EDGE",EDGE,{"disambiguationData":[OSD([sQuery(id+"F0.wireOp",EDGE,"E22")])],"isStart":true});
            var Q11;
            {var subQ0=sQuery(id+"F0.wireOp",EDGE,"E21");var subQ1=sQuery(id+"F0.wireOp",EDGE,"E17");Q11=makeQuery(id+"F2.opFillet","BLEND_EDGE",EDGE,{"blendedFrom":[makeQuery(id+"F1.opExtrude","SWEPT_EDGE",EDGE,{"disambiguationData":[OSD([subQ1,subQ0])]}),makeQuery(id+"F1.opExtrude","CAP_FACE",FACE,{"disambiguationData":[OSD([sQuery(id+"F0.wireOp",EDGE,"E0"),sQuery(id+"F0.wireOp",EDGE,"E1"),sQuery(id+"F0.wireOp",EDGE,"E3"),sQuery(id+"F0.wireOp",EDGE,"E4"),sQuery(id+"F0.wireOp",EDGE,"E5"),sQuery(id+"F0.wireOp",EDGE,"E6"),sQuery(id+"F0.wireOp",EDGE,"E7.MirrorCS"),sQuery(id+"F0.wireOp",EDGE,"E8.MirrorCS"),sQuery(id+"F0.wireOp",EDGE,"E9.MirrorCS"),sQuery(id+"F0.wireOp",EDGE,"E10.MirrorCS"),sQuery(id+"F0.wireOp",EDGE,"E11.MirrorCS"),sQuery(id+"F0.wireOp",EDGE,"E14.trimOffspring"),subQ1,sQuery(id+"F0.wireOp",EDGE,"E18"),sQuery(id+"F0.wireOp",EDGE,"E19"),sQuery(id+"F0.wireOp",EDGE,"E20"),subQ0,sQuery(id+"F0.wireOp",EDGE,"E22"),sQuery(id+"F0.wireOp",EDGE,"E23")])],"isStart":true})],"blendedInto":[makeQuery(id+"F1.opExtrude","CAP_FACE",FACE,{"disambiguationData":[OSD([sQuery(id+"F0.wireOp",EDGE,"E0"),sQuery(id+"F0.wireOp",EDGE,"E1"),sQuery(id+"F0.wireOp",EDGE,"E3"),sQuery(id+"F0.wireOp",EDGE,"E4"),sQuery(id+"F0.wireOp",EDGE,"E5"),sQuery(id+"F0.wireOp",EDGE,"E6"),sQuery(id+"F0.wireOp",EDGE,"E7.MirrorCS"),sQuery(id+"F0.wireOp",EDGE,"E8.MirrorCS"),sQuery(id+"F0.wireOp",EDGE,"E9.MirrorCS"),sQuery(id+"F0.wireOp",EDGE,"E10.MirrorCS"),sQuery(id+"F0.wireOp",EDGE,"E11.MirrorCS"),sQuery(id+"F0.wireOp",EDGE,"E14.trimOffspring"),subQ1,sQuery(id+"F0.wireOp",EDGE,"E18"),sQuery(id+"F0.wireOp",EDGE,"E19"),sQuery(id+"F0.wireOp",EDGE,"E20"),subQ0,sQuery(id+"F0.wireOp",EDGE,"E22"),sQuery(id+"F0.wireOp",EDGE,"E23")])],"isStart":true})]});}
            var Q12;
            Q12=makeQuery(id+"F1.opExtrude","CAP_EDGE",EDGE,{"disambiguationData":[OSD([sQuery(id+"F0.wireOp",EDGE,"E17")])],"isStart":true});
            var Q13;
            {var subQ0=sQuery(id+"F0.wireOp",EDGE,"E23");var subQ1=sQuery(id+"F0.wireOp",EDGE,"E17");Q13=makeQuery(id+"F2.opFillet","BLEND_EDGE",EDGE,{"blendedFrom":[makeQuery(id+"F1.opExtrude","SWEPT_EDGE",EDGE,{"disambiguationData":[OSD([subQ1,subQ0])]}),makeQuery(id+"F1.opExtrude","CAP_FACE",FACE,{"disambiguationData":[OSD([sQuery(id+"F0.wireOp",EDGE,"E0"),sQuery(id+"F0.wireOp",EDGE,"E1"),sQuery(id+"F0.wireOp",EDGE,"E3"),sQuery(id+"F0.wireOp",EDGE,"E4"),sQuery(id+"F0.wireOp",EDGE,"E5"),sQuery(id+"F0.wireOp",EDGE,"E6"),sQuery(id+"F0.wireOp",EDGE,"E7.MirrorCS"),sQuery(id+"F0.wireOp",EDGE,"E8.MirrorCS"),sQuery(id+"F0.wireOp",EDGE,"E9.MirrorCS"),sQuery(id+"F0.wireOp",EDGE,"E10.MirrorCS"),sQuery(id+"F0.wireOp",EDGE,"E11.MirrorCS"),sQuery(id+"F0.wireOp",EDGE,"E14.trimOffspring"),subQ1,sQuery(id+"F0.wireOp",EDGE,"E18"),sQuery(id+"F0.wireOp",EDGE,"E19"),sQuery(id+"F0.wireOp",EDGE,"E20"),sQuery(id+"F0.wireOp",EDGE,"E21"),sQuery(id+"F0.wireOp",EDGE,"E22"),subQ0])],"isStart":true})],"blendedInto":[makeQuery(id+"F1.opExtrude","CAP_FACE",FACE,{"disambiguationData":[OSD([sQuery(id+"F0.wireOp",EDGE,"E0"),sQuery(id+"F0.wireOp",EDGE,"E1"),sQuery(id+"F0.wireOp",EDGE,"E3"),sQuery(id+"F0.wireOp",EDGE,"E4"),sQuery(id+"F0.wireOp",EDGE,"E5"),sQuery(id+"F0.wireOp",EDGE,"E6"),sQuery(id+"F0.wireOp",EDGE,"E7.MirrorCS"),sQuery(id+"F0.wireOp",EDGE,"E8.MirrorCS"),sQuery(id+"F0.wireOp",EDGE,"E9.MirrorCS"),sQuery(id+"F0.wireOp",EDGE,"E10.MirrorCS"),sQuery(id+"F0.wireOp",EDGE,"E11.MirrorCS"),sQuery(id+"F0.wireOp",EDGE,"E14.trimOffspring"),subQ1,sQuery(id+"F0.wireOp",EDGE,"E18"),sQuery(id+"F0.wireOp",EDGE,"E19"),sQuery(id+"F0.wireOp",EDGE,"E20"),sQuery(id+"F0.wireOp",EDGE,"E21"),sQuery(id+"F0.wireOp",EDGE,"E22"),subQ0])],"isStart":true})]});}
            var Q14;
            Q14=makeQuery(id+"F1.opExtrude","CAP_EDGE",EDGE,{"disambiguationData":[OSD([sQuery(id+"F0.wireOp",EDGE,"E23")])],"isStart":true});
            var Q15;
            {var subQ0=sQuery(id+"F0.wireOp",EDGE,"E23");var subQ1=sQuery(id+"F0.wireOp",EDGE,"E22");Q15=makeQuery(id+"F2.opFillet","BLEND_EDGE",EDGE,{"blendedFrom":[makeQuery(id+"F1.opExtrude","SWEPT_EDGE",EDGE,{"disambiguationData":[OSD([subQ1,subQ0])]}),makeQuery(id+"F1.opExtrude","CAP_FACE",FACE,{"disambiguationData":[OSD([sQuery(id+"F0.wireOp",EDGE,"E0"),sQuery(id+"F0.wireOp",EDGE,"E1"),sQuery(id+"F0.wireOp",EDGE,"E3"),sQuery(id+"F0.wireOp",EDGE,"E4"),sQuery(id+"F0.wireOp",EDGE,"E5"),sQuery(id+"F0.wireOp",EDGE,"E6"),sQuery(id+"F0.wireOp",EDGE,"E7.MirrorCS"),sQuery(id+"F0.wireOp",EDGE,"E8.MirrorCS"),sQuery(id+"F0.wireOp",EDGE,"E9.MirrorCS"),sQuery(id+"F0.wireOp",EDGE,"E10.MirrorCS"),sQuery(id+"F0.wireOp",EDGE,"E11.MirrorCS"),sQuery(id+"F0.wireOp",EDGE,"E14.trimOffspring"),sQuery(id+"F0.wireOp",EDGE,"E17"),sQuery(id+"F0.wireOp",EDGE,"E18"),sQuery(id+"F0.wireOp",EDGE,"E19"),sQuery(id+"F0.wireOp",EDGE,"E20"),sQuery(id+"F0.wireOp",EDGE,"E21"),subQ1,subQ0])],"isStart":true})],"blendedInto":[makeQuery(id+"F1.opExtrude","CAP_FACE",FACE,{"disambiguationData":[OSD([sQuery(id+"F0.wireOp",EDGE,"E0"),sQuery(id+"F0.wireOp",EDGE,"E1"),sQuery(id+"F0.wireOp",EDGE,"E3"),sQuery(id+"F0.wireOp",EDGE,"E4"),sQuery(id+"F0.wireOp",EDGE,"E5"),sQuery(id+"F0.wireOp",EDGE,"E6"),sQuery(id+"F0.wireOp",EDGE,"E7.MirrorCS"),sQuery(id+"F0.wireOp",EDGE,"E8.MirrorCS"),sQuery(id+"F0.wireOp",EDGE,"E9.MirrorCS"),sQuery(id+"F0.wireOp",EDGE,"E10.MirrorCS"),sQuery(id+"F0.wireOp",EDGE,"E11.MirrorCS"),sQuery(id+"F0.wireOp",EDGE,"E14.trimOffspring"),sQuery(id+"F0.wireOp",EDGE,"E17"),sQuery(id+"F0.wireOp",EDGE,"E18"),sQuery(id+"F0.wireOp",EDGE,"E19"),sQuery(id+"F0.wireOp",EDGE,"E20"),sQuery(id+"F0.wireOp",EDGE,"E21"),subQ1,subQ0])],"isStart":true})]});}
            fillet(context, id + "F14", {"entities" : qUnion([Q0, Q1, Q2, Q3, Q4, Q5, Q6, Q7, Q8, Q9, Q10, Q11, Q12, Q13, Q14, Q15]), "tangentPropagation" : true, "crossSection" : FilletCrossSection.CURVATURE, "radius" : 1 * mm, "magnitude" : 0.1, "defaultsChanged" : true, "vertexSettings" : []});
        }
    });
